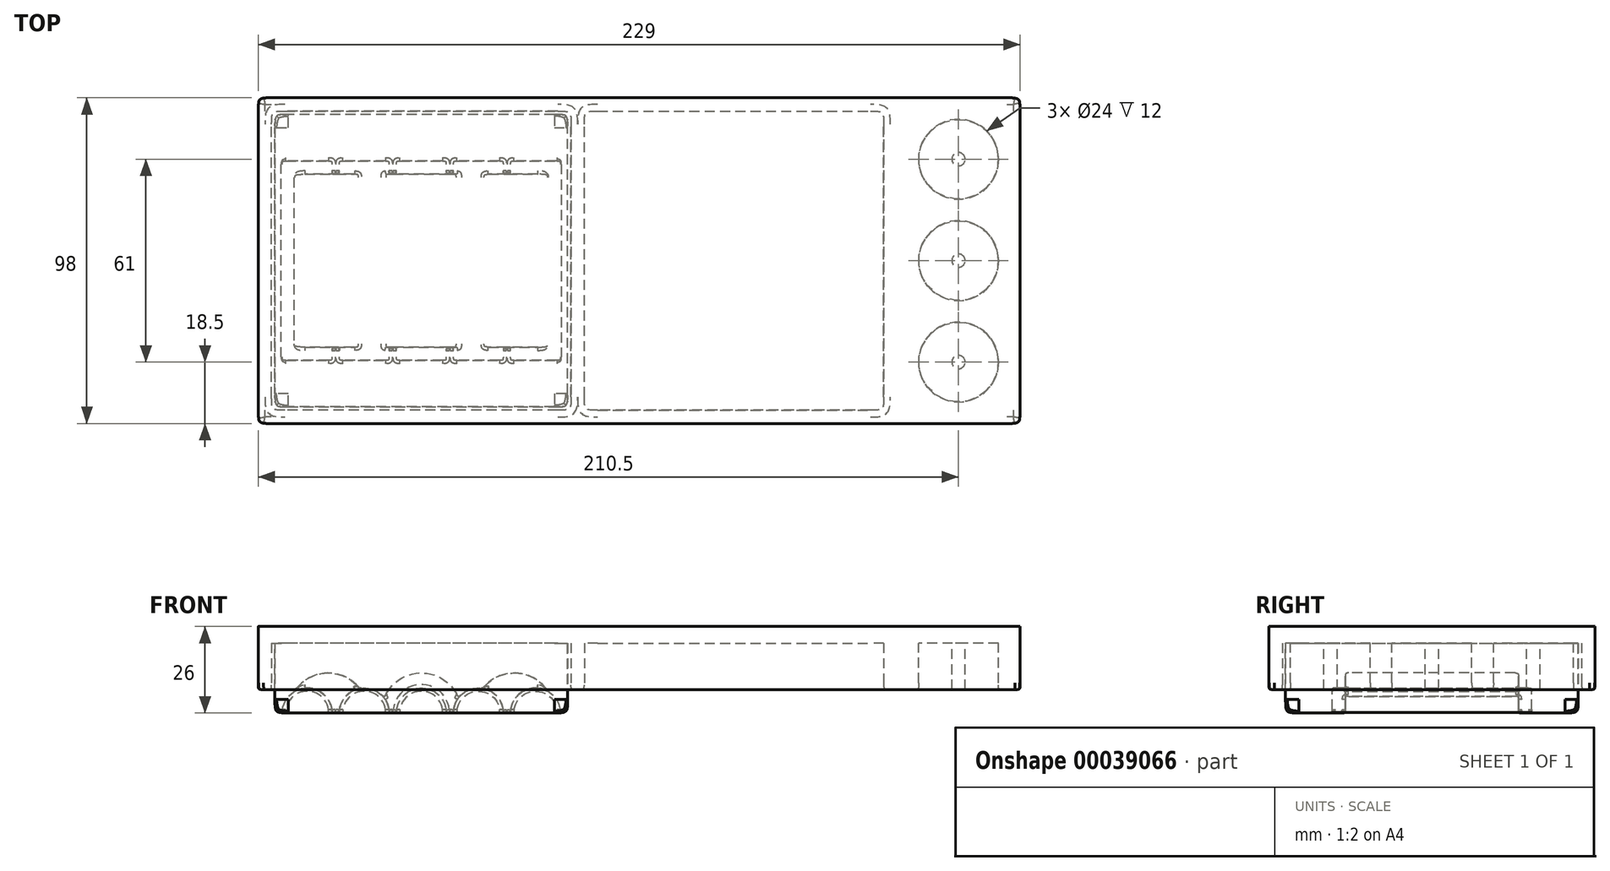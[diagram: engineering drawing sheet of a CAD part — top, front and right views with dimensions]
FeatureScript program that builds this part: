
annotation { "Feature Type Name" : "Feature", "Feature Type Description" : "" }
export const myFeature = defineFeature(function(context is Context, id is Id, definition is map)
    precondition{}
    {
        {
            var Q0;
            Q0=qCreatedBy(makeId("Top.planeOp"),FACE);
            var sketch = newSketch(context, id + "F0", { "sketchPlane" : qUnion([Q0])});
            skLineSegment(sketch, "E0.rect.bottom", {"start": v(44, -44) * mm, "end": v(-44, -44) * mm});
            skLineSegment(sketch, "E0.rect.top", {"start": v(44, 44) * mm, "end": v(-44, 44) * mm});
            skLineSegment(sketch, "E0.rect.left", {"start": v(44, -44) * mm, "end": v(44, 44) * mm});
            skLineSegment(sketch, "E0.rect.right", {"start": v(-44, -44) * mm, "end": v(-44, 44) * mm});
            skPoint(sketch, "E0.rect.middle", {"position": v(0, 0) * mm});
            skLineSegment(sketch, "E1.rect.bottom", {"start": v(12, -26) * mm, "end": v(-12, -26) * mm});
            skLineSegment(sketch, "E1.rect.top", {"start": v(12, 26) * mm, "end": v(-12, 26) * mm});
            skLineSegment(sketch, "E1.rect.left", {"start": v(12, -26) * mm, "end": v(12, 26) * mm});
            skLineSegment(sketch, "E1.rect.right", {"start": v(-12, -26) * mm, "end": v(-12, 26) * mm});
            skLineSegment(sketch, "E2.rect.bottom", {"start": v(40, -26) * mm, "end": v(16, -26) * mm});
            skLineSegment(sketch, "E2.rect.top", {"start": v(40, 26) * mm, "end": v(16, 26) * mm});
            skLineSegment(sketch, "E2.rect.left", {"start": v(40, -26) * mm, "end": v(40, 26) * mm});
            skLineSegment(sketch, "E2.rect.right", {"start": v(16, -26) * mm, "end": v(16, 26) * mm});
            skPoint(sketch, "E2.rect.middle", {"position": v(28, 0) * mm});
            skLineSegment(sketch, "E3.rect.bottom", {"start": v(-16, -26) * mm, "end": v(-40, -26) * mm});
            skLineSegment(sketch, "E3.rect.top", {"start": v(-16, 26) * mm, "end": v(-40, 26) * mm});
            skLineSegment(sketch, "E3.rect.left", {"start": v(-16, -26) * mm, "end": v(-16, 26) * mm});
            skLineSegment(sketch, "E3.rect.right", {"start": v(-40, -26) * mm, "end": v(-40, 26) * mm});
            skPoint(sketch, "E3.rect.middle", {"position": v(-28, 0) * mm});
            skLineSegment(sketch, "E4.rect.bottom", {"start": v(-7.5, -30) * mm, "end": v(7.5, -30) * mm});
            skLineSegment(sketch, "E4.rect.top", {"start": v(-7.5, 30) * mm, "end": v(7.5, 30) * mm});
            skLineSegment(sketch, "E4.rect.left", {"start": v(-7.5, -30) * mm, "end": v(-7.5, 30) * mm});
            skLineSegment(sketch, "E4.rect.right", {"start": v(7.5, -30) * mm, "end": v(7.5, 30) * mm});
            skLineSegment(sketch, "E5.rect.bottom", {"start": v(24.66, -30) * mm, "end": v(9.66, -30) * mm});
            skLineSegment(sketch, "E5.rect.top", {"start": v(24.66, 30) * mm, "end": v(9.66, 30) * mm});
            skLineSegment(sketch, "E5.rect.left", {"start": v(24.66, -30) * mm, "end": v(24.66, 30) * mm});
            skLineSegment(sketch, "E5.rect.right", {"start": v(9.66, -30) * mm, "end": v(9.66, 30) * mm});
            skPoint(sketch, "E5.rect.middle", {"position": v(17.16, 0) * mm});
            skLineSegment(sketch, "E6.rect.bottom", {"start": v(26.82, -30) * mm, "end": v(41.82, -30) * mm});
            skLineSegment(sketch, "E6.rect.top", {"start": v(26.82, 30) * mm, "end": v(41.82, 30) * mm});
            skLineSegment(sketch, "E6.rect.left", {"start": v(26.82, -30) * mm, "end": v(26.82, 30) * mm});
            skLineSegment(sketch, "E6.rect.right", {"start": v(41.82, -30) * mm, "end": v(41.82, 30) * mm});
            skPoint(sketch, "E6.rect.middle", {"position": v(34.32, 0) * mm});
            skLineSegment(sketch, "E7.rect.bottom", {"start": v(-9.66, -30) * mm, "end": v(-24.66, -30) * mm});
            skLineSegment(sketch, "E7.rect.top", {"start": v(-9.66, 30) * mm, "end": v(-24.66, 30) * mm});
            skLineSegment(sketch, "E7.rect.left", {"start": v(-9.66, -30) * mm, "end": v(-9.66, 30) * mm});
            skLineSegment(sketch, "E7.rect.right", {"start": v(-24.66, -30) * mm, "end": v(-24.66, 30) * mm});
            skPoint(sketch, "E7.rect.middle", {"position": v(-17.16, 0) * mm});
            skLineSegment(sketch, "E8.rect.bottom", {"start": v(-26.82, -30) * mm, "end": v(-41.82, -30) * mm});
            skLineSegment(sketch, "E8.rect.top", {"start": v(-26.82, 30) * mm, "end": v(-41.82, 30) * mm});
            skLineSegment(sketch, "E8.rect.left", {"start": v(-26.82, -30) * mm, "end": v(-26.82, 30) * mm});
            skLineSegment(sketch, "E8.rect.right", {"start": v(-41.82, -30) * mm, "end": v(-41.82, 30) * mm});
            skPoint(sketch, "E8.rect.middle", {"position": v(-34.32, 0) * mm});
            skLineSegment(sketch, "E9", {"start": v(44, 0) * mm, "end": v(41.82, 0) * mm, "construction": true});
            skLineSegment(sketch, "E10", {"start": v(26.82, 0) * mm, "end": v(24.66, 0) * mm, "construction": true});
            skLineSegment(sketch, "E11", {"start": v(9.66, 0) * mm, "end": v(7.5, 0) * mm, "construction": true});
            skLineSegment(sketch, "E12", {"start": v(-7.5, 0) * mm, "end": v(-9.66, 0) * mm, "construction": true});
            skLineSegment(sketch, "E13", {"start": v(-24.66, 0) * mm, "end": v(-26.82, 0) * mm, "construction": true});
            skLineSegment(sketch, "E14", {"start": v(-41.82, 0) * mm, "end": v(-44, 0) * mm, "construction": true});
            skSolve(sketch);
        }
        {
            var Q0;
            Q0=makeQuery(id+"F0.imprint","IMPRINT",FACE,{"disambiguationData":[TD([[makeQuery(id+"F0.imprint","IMPRINT",EDGE,{"derivedFrom":sQuery(id+"F0.wireOp",EDGE,"E0.rect.bottom")}),-1.0]])]});
            var Q1;
            {var subQ6=sQuery(id+"F0.wireOp",EDGE,"E2.rect.left");Q1=makeQuery(id+"F0.imprint","IMPRINT",FACE,{"disambiguationData":[TD([[makeQuery(id+"F0.imprint","IMPRINT",EDGE,{"derivedFrom":subQ6}),-1.0]])]});}
            var Q2;
            {var subQ5=sQuery(id+"F0.wireOp",EDGE,"E2.rect.left");Q2=makeQuery(id+"F0.imprint","IMPRINT",FACE,{"disambiguationData":[TD([[makeQuery(id+"F0.imprint","IMPRINT",EDGE,{"derivedFrom":subQ5}),1.0]])]});}
            var Q3;
            {var subQ3=sQuery(id+"F0.wireOp",EDGE,"E2.rect.bottom");var subQ5=sQuery(id+"F0.wireOp",EDGE,"E6.rect.left");var subQ7=makeQuery(id+"F0.imprint","INTERSECT",VERTEX,{"derivedFrom":[subQ3,subQ5]});Q3=makeQuery(id+"F0.imprint","IMPRINT",FACE,{"disambiguationData":[TD([[makeQuery(id+"F0.imprint","IMPRINT",EDGE,{"disambiguationData":[TD([[subQ7,-1.0]])],"derivedFrom":subQ3}),-1.0]])]});}
            var Q4;
            {var subQ11=sQuery(id+"F0.wireOp",EDGE,"E1.rect.left");Q4=makeQuery(id+"F0.imprint","IMPRINT",FACE,{"disambiguationData":[TD([[makeQuery(id+"F0.imprint","IMPRINT",EDGE,{"derivedFrom":subQ11}),-1.0]])]});}
            var Q5;
            {var subQ5=sQuery(id+"F0.wireOp",EDGE,"E2.rect.right");Q5=makeQuery(id+"F0.imprint","IMPRINT",FACE,{"disambiguationData":[TD([[makeQuery(id+"F0.imprint","IMPRINT",EDGE,{"derivedFrom":subQ5}),-1.0]])]});}
            var Q6;
            {var subQ5=sQuery(id+"F0.wireOp",EDGE,"E1.rect.left");Q6=makeQuery(id+"F0.imprint","IMPRINT",FACE,{"disambiguationData":[TD([[makeQuery(id+"F0.imprint","IMPRINT",EDGE,{"derivedFrom":subQ5}),1.0]])]});}
            var Q7;
            {var subQ0=sQuery(id+"F0.wireOp",EDGE,"E5.rect.right");var subQ3=sQuery(id+"F0.wireOp",EDGE,"E1.rect.bottom");var subQ4=makeQuery(id+"F0.imprint","INTERSECT",VERTEX,{"derivedFrom":[subQ3,subQ0]});Q7=makeQuery(id+"F0.imprint","IMPRINT",FACE,{"disambiguationData":[TD([[makeQuery(id+"F0.imprint","IMPRINT",EDGE,{"disambiguationData":[TD([[subQ4,-1.0]])],"derivedFrom":subQ3}),-1.0]])]});}
            var Q8;
            {var subQ0=sQuery(id+"F0.wireOp",EDGE,"E4.rect.right");var subQ3=sQuery(id+"F0.wireOp",EDGE,"E1.rect.bottom");var subQ4=makeQuery(id+"F0.imprint","INTERSECT",VERTEX,{"derivedFrom":[subQ3,subQ0]});Q8=makeQuery(id+"F0.imprint","IMPRINT",FACE,{"disambiguationData":[TD([[makeQuery(id+"F0.imprint","IMPRINT",EDGE,{"disambiguationData":[TD([[subQ4,-1.0]])],"derivedFrom":subQ3}),-1.0]])]});}
            var Q9;
            {var subQ0=sQuery(id+"F0.wireOp",EDGE,"E4.rect.bottom");Q9=makeQuery(id+"F0.imprint","IMPRINT",FACE,{"disambiguationData":[TD([[makeQuery(id+"F0.imprint","IMPRINT",EDGE,{"derivedFrom":subQ0}),1.0]])]});}
            var Q10;
            {var subQ3=sQuery(id+"F0.wireOp",EDGE,"E4.rect.top");Q10=makeQuery(id+"F0.imprint","IMPRINT",FACE,{"disambiguationData":[TD([[makeQuery(id+"F0.imprint","IMPRINT",EDGE,{"derivedFrom":subQ3}),-1.0]])]});}
            var Q11;
            {var subQ3=sQuery(id+"F0.wireOp",EDGE,"E1.rect.bottom");var subQ5=sQuery(id+"F0.wireOp",EDGE,"E4.rect.left");var subQ7=makeQuery(id+"F0.imprint","INTERSECT",VERTEX,{"derivedFrom":[subQ3,subQ5]});Q11=makeQuery(id+"F0.imprint","IMPRINT",FACE,{"disambiguationData":[TD([[makeQuery(id+"F0.imprint","IMPRINT",EDGE,{"disambiguationData":[TD([[subQ7,-1.0]])],"derivedFrom":subQ3}),-1.0]])]});}
            var Q12;
            {var subQ5=sQuery(id+"F0.wireOp",EDGE,"E1.rect.right");Q12=makeQuery(id+"F0.imprint","IMPRINT",FACE,{"disambiguationData":[TD([[makeQuery(id+"F0.imprint","IMPRINT",EDGE,{"derivedFrom":subQ5}),-1.0]])]});}
            var Q13;
            {var subQ5=sQuery(id+"F0.wireOp",EDGE,"E1.rect.right");Q13=makeQuery(id+"F0.imprint","IMPRINT",FACE,{"disambiguationData":[TD([[makeQuery(id+"F0.imprint","IMPRINT",EDGE,{"derivedFrom":subQ5}),1.0]])]});}
            var Q14;
            {var subQ5=sQuery(id+"F0.wireOp",EDGE,"E3.rect.left");Q14=makeQuery(id+"F0.imprint","IMPRINT",FACE,{"disambiguationData":[TD([[makeQuery(id+"F0.imprint","IMPRINT",EDGE,{"derivedFrom":subQ5}),1.0]])]});}
            var Q15;
            {var subQ3=sQuery(id+"F0.wireOp",EDGE,"E3.rect.bottom");var subQ5=sQuery(id+"F0.wireOp",EDGE,"E7.rect.right");var subQ7=makeQuery(id+"F0.imprint","INTERSECT",VERTEX,{"derivedFrom":[subQ3,subQ5]});Q15=makeQuery(id+"F0.imprint","IMPRINT",FACE,{"disambiguationData":[TD([[makeQuery(id+"F0.imprint","IMPRINT",EDGE,{"disambiguationData":[TD([[subQ7,-1.0]])],"derivedFrom":subQ3}),-1.0]])]});}
            var Q16;
            {var subQ5=sQuery(id+"F0.wireOp",EDGE,"E3.rect.right");Q16=makeQuery(id+"F0.imprint","IMPRINT",FACE,{"disambiguationData":[TD([[makeQuery(id+"F0.imprint","IMPRINT",EDGE,{"derivedFrom":subQ5}),-1.0]])]});}
            var Q17;
            {var subQ7=sQuery(id+"F0.wireOp",EDGE,"E3.rect.right");Q17=makeQuery(id+"F0.imprint","IMPRINT",FACE,{"disambiguationData":[TD([[makeQuery(id+"F0.imprint","IMPRINT",EDGE,{"derivedFrom":subQ7}),1.0]])]});}
            extrude(context, id + "F1", {"entities" : qUnion([Q0, Q1, Q2, Q3, Q4, Q5, Q6, Q7, Q8, Q9, Q10, Q11, Q12, Q13, Q14, Q15, Q16, Q17]), "depth" : 21 * mm});
        }
        {
            var Q0;
            Q0=makeQuery(id+"F0.imprint","IMPRINT",FACE,{"disambiguationData":[TD([[makeQuery(id+"F0.imprint","IMPRINT",EDGE,{"derivedFrom":sQuery(id+"F0.wireOp",EDGE,"E0.rect.bottom")}),-1.0]])]});
            var sketch = newSketch(context, id + "F2", { "sketchPlane" : qUnion([Q0])});
            skLineSegment(sketch, "E15.rect.bottom", {"start": v(16, -26) * mm, "end": v(40, -26) * mm});
            skLineSegment(sketch, "E15.rect.top", {"start": v(16, 26) * mm, "end": v(40, 26) * mm});
            skLineSegment(sketch, "E15.rect.left", {"start": v(16, -26) * mm, "end": v(16, 26) * mm});
            skLineSegment(sketch, "E15.rect.right", {"start": v(40, -26) * mm, "end": v(40, 26) * mm});
            skPoint(sketch, "E15.rect.middle", {"position": v(28, 0) * mm});
            skLineSegment(sketch, "E16.rect.bottom", {"start": v(12, -26) * mm, "end": v(-12, -26) * mm});
            skLineSegment(sketch, "E16.rect.top", {"start": v(12, 26) * mm, "end": v(-12, 26) * mm});
            skLineSegment(sketch, "E16.rect.left", {"start": v(12, -26) * mm, "end": v(12, 26) * mm});
            skLineSegment(sketch, "E16.rect.right", {"start": v(-12, -26) * mm, "end": v(-12, 26) * mm});
            skPoint(sketch, "E16.rect.middle", {"position": v(0, 0) * mm});
            skLineSegment(sketch, "E17.rect.bottom", {"start": v(-40, 26) * mm, "end": v(-16, 26) * mm});
            skLineSegment(sketch, "E17.rect.top", {"start": v(-40, -26) * mm, "end": v(-16, -26) * mm});
            skLineSegment(sketch, "E17.rect.left", {"start": v(-40, 26) * mm, "end": v(-40, -26) * mm});
            skLineSegment(sketch, "E17.rect.right", {"start": v(-16, 26) * mm, "end": v(-16, -26) * mm});
            skPoint(sketch, "E17.rect.middle", {"position": v(-28, 0) * mm});
            skLineSegment(sketch, "E18", {"start": v(28, 26) * mm, "end": v(28, -26) * mm});
            skLineSegment(sketch, "E19", {"start": v(0, 26) * mm, "end": v(0, -26) * mm});
            skLineSegment(sketch, "E20", {"start": v(-28, 26) * mm, "end": v(-28, -26) * mm});
            skSolve(sketch);
        }
        {
            var Q0;
            {var subQ2=sQuery(id+"F2.wireOp",EDGE,"E15.rect.right");Q0=makeQuery(id+"F2.imprint","IMPRINT",FACE,{"disambiguationData":[TD([[makeQuery(id+"F2.imprint","IMPRINT",EDGE,{"derivedFrom":subQ2}),1.0]])]});}
            var Q1;
            Q1=sQuery(id+"F2.wireOp",EDGE,"E18");
            revolve(context, id + "F3", {"operationType" : NewBodyOperationType.REMOVE, "entities" : qUnion([Q0]), "axis" : qUnion([Q1]), "revolveType" : RevolveType.FULL, "oppositeDirection" : true});
        }
        {
            var Q0;
            {var subQ1=sQuery(id+"F2.wireOp",EDGE,"E16.rect.left");Q0=makeQuery(id+"F2.imprint","IMPRINT",FACE,{"disambiguationData":[TD([[makeQuery(id+"F2.imprint","IMPRINT",EDGE,{"derivedFrom":subQ1}),1.0]])]});}
            var Q1;
            Q1=sQuery(id+"F2.wireOp",EDGE,"E19");
            revolve(context, id + "F4", {"operationType" : NewBodyOperationType.REMOVE, "entities" : qUnion([Q0]), "axis" : qUnion([Q1]), "revolveType" : RevolveType.FULL, "oppositeDirection" : true});
        }
        {
            var Q0;
            {var subQ0=sQuery(id+"F2.wireOp",EDGE,"E17.rect.right");Q0=makeQuery(id+"F2.imprint","IMPRINT",FACE,{"disambiguationData":[TD([[makeQuery(id+"F2.imprint","IMPRINT",EDGE,{"derivedFrom":subQ0}),-1.0]])]});}
            var Q1;
            Q1=sQuery(id+"F2.wireOp",EDGE,"E20");
            revolve(context, id + "F5", {"operationType" : NewBodyOperationType.REMOVE, "entities" : qUnion([Q0]), "axis" : qUnion([Q1]), "revolveType" : RevolveType.FULL, "oppositeDirection" : true});
        }
        {
            var Q0;
            Q0=makeQuery(id+"F0.imprint","IMPRINT",FACE,{"disambiguationData":[TD([[makeQuery(id+"F0.imprint","IMPRINT",EDGE,{"derivedFrom":sQuery(id+"F0.wireOp",EDGE,"E0.rect.bottom")}),-1.0]])]});
            var sketch = newSketch(context, id + "F6", { "sketchPlane" : qUnion([Q0])});
            skLineSegment(sketch, "E21.rect.bottom", {"start": v(41.82, 30) * mm, "end": v(26.82, 30) * mm});
            skLineSegment(sketch, "E21.rect.top", {"start": v(41.82, -30) * mm, "end": v(26.82, -30) * mm});
            skLineSegment(sketch, "E21.rect.left", {"start": v(41.82, 30) * mm, "end": v(41.82, -30) * mm});
            skLineSegment(sketch, "E21.rect.right", {"start": v(26.82, 30) * mm, "end": v(26.82, -30) * mm});
            skPoint(sketch, "E21.rect.middle", {"position": v(34.32, 0) * mm});
            skLineSegment(sketch, "E22.rect.bottom", {"start": v(24.66, 30) * mm, "end": v(9.66, 30) * mm});
            skLineSegment(sketch, "E22.rect.top", {"start": v(24.66, -30) * mm, "end": v(9.66, -30) * mm});
            skLineSegment(sketch, "E22.rect.left", {"start": v(24.66, 30) * mm, "end": v(24.66, -30) * mm});
            skLineSegment(sketch, "E22.rect.right", {"start": v(9.66, 30) * mm, "end": v(9.66, -30) * mm});
            skPoint(sketch, "E22.rect.middle", {"position": v(17.16, 0) * mm});
            skLineSegment(sketch, "E23.rect.bottom", {"start": v(-7.5, 30) * mm, "end": v(7.5, 30) * mm});
            skLineSegment(sketch, "E23.rect.top", {"start": v(-7.5, -30) * mm, "end": v(7.5, -30) * mm});
            skLineSegment(sketch, "E23.rect.left", {"start": v(-7.5, 30) * mm, "end": v(-7.5, -30) * mm});
            skLineSegment(sketch, "E23.rect.right", {"start": v(7.5, 30) * mm, "end": v(7.5, -30) * mm});
            skPoint(sketch, "E23.rect.middle", {"position": v(0, 0) * mm});
            skLineSegment(sketch, "E24.rect.bottom", {"start": v(-24.66, 30) * mm, "end": v(-9.66, 30) * mm});
            skLineSegment(sketch, "E24.rect.top", {"start": v(-24.66, -30) * mm, "end": v(-9.66, -30) * mm});
            skLineSegment(sketch, "E24.rect.left", {"start": v(-24.66, 30) * mm, "end": v(-24.66, -30) * mm});
            skLineSegment(sketch, "E24.rect.right", {"start": v(-9.66, 30) * mm, "end": v(-9.66, -30) * mm});
            skPoint(sketch, "E24.rect.middle", {"position": v(-17.16, 0) * mm});
            skLineSegment(sketch, "E25.rect.bottom", {"start": v(-41.82, 30) * mm, "end": v(-26.82, 30) * mm});
            skLineSegment(sketch, "E25.rect.top", {"start": v(-41.82, -30) * mm, "end": v(-26.82, -30) * mm});
            skLineSegment(sketch, "E25.rect.left", {"start": v(-41.82, 30) * mm, "end": v(-41.82, -30) * mm});
            skLineSegment(sketch, "E25.rect.right", {"start": v(-26.82, 30) * mm, "end": v(-26.82, -30) * mm});
            skPoint(sketch, "E25.rect.middle", {"position": v(-34.32, 0) * mm});
            skLineSegment(sketch, "E26", {"start": v(34.32, 30) * mm, "end": v(34.32, -30) * mm});
            skLineSegment(sketch, "E27", {"start": v(17.16, -30) * mm, "end": v(17.16, 30) * mm});
            skLineSegment(sketch, "E28", {"start": v(0, -30) * mm, "end": v(0, 30) * mm});
            skLineSegment(sketch, "E29", {"start": v(-17.16, -30) * mm, "end": v(-17.16, 30) * mm});
            skLineSegment(sketch, "E30", {"start": v(-34.32, -30) * mm, "end": v(-34.32, 30) * mm});
            skSolve(sketch);
        }
        {
            var Q0;
            {var subQ8=sQuery(id+"F6.wireOp",EDGE,"E26");Q0=makeQuery(id+"F6.imprint","IMPRINT",FACE,{"disambiguationData":[TD([[makeQuery(id+"F6.imprint","IMPRINT",EDGE,{"derivedFrom":subQ8}),-1.0]])]});}
            var Q1;
            Q1=sQuery(id+"F6.wireOp",EDGE,"E26");
            revolve(context, id + "F7", {"operationType" : NewBodyOperationType.REMOVE, "entities" : qUnion([Q0]), "axis" : qUnion([Q1]), "revolveType" : RevolveType.FULL, "oppositeDirection" : true});
        }
        {
            var Q0;
            {var subQ8=sQuery(id+"F6.wireOp",EDGE,"E27");Q0=makeQuery(id+"F6.imprint","IMPRINT",FACE,{"disambiguationData":[TD([[makeQuery(id+"F6.imprint","IMPRINT",EDGE,{"derivedFrom":subQ8}),1.0]])]});}
            var Q1;
            Q1=sQuery(id+"F6.wireOp",EDGE,"E27");
            revolve(context, id + "F8", {"operationType" : NewBodyOperationType.REMOVE, "entities" : qUnion([Q0]), "axis" : qUnion([Q1]), "revolveType" : RevolveType.FULL, "oppositeDirection" : true});
        }
        {
            var Q0;
            {var subQ0=sQuery(id+"F6.wireOp",EDGE,"E28");Q0=makeQuery(id+"F6.imprint","IMPRINT",FACE,{"disambiguationData":[TD([[makeQuery(id+"F6.imprint","IMPRINT",EDGE,{"derivedFrom":subQ0}),1.0]])]});}
            var Q1;
            Q1=sQuery(id+"F6.wireOp",EDGE,"E28");
            revolve(context, id + "F9", {"operationType" : NewBodyOperationType.REMOVE, "entities" : qUnion([Q0]), "axis" : qUnion([Q1]), "revolveType" : RevolveType.FULL, "oppositeDirection" : true});
        }
        {
            var Q0;
            {var subQ7=sQuery(id+"F6.wireOp",EDGE,"E29");Q0=makeQuery(id+"F6.imprint","IMPRINT",FACE,{"disambiguationData":[TD([[makeQuery(id+"F6.imprint","IMPRINT",EDGE,{"derivedFrom":subQ7}),-1.0]])]});}
            var Q1;
            Q1=sQuery(id+"F6.wireOp",EDGE,"E29");
            revolve(context, id + "F10", {"operationType" : NewBodyOperationType.REMOVE, "entities" : qUnion([Q0]), "axis" : qUnion([Q1]), "revolveType" : RevolveType.FULL, "oppositeDirection" : true});
        }
        {
            var Q0;
            {var subQ8=sQuery(id+"F6.wireOp",EDGE,"E30");Q0=makeQuery(id+"F6.imprint","IMPRINT",FACE,{"disambiguationData":[TD([[makeQuery(id+"F6.imprint","IMPRINT",EDGE,{"derivedFrom":subQ8}),-1.0]])]});}
            var Q1;
            Q1=sQuery(id+"F6.wireOp",EDGE,"E30");
            revolve(context, id + "F11", {"operationType" : NewBodyOperationType.REMOVE, "entities" : qUnion([Q0]), "axis" : qUnion([Q1]), "revolveType" : RevolveType.FULL, "oppositeDirection" : true});
        }
        {
            var Q0;
            Q0=makeQuery(id+"F10.boolean.opBoolean","INTERSECT",EDGE,{"derivedFrom":[makeQuery(id+"F5.boolean.opBoolean","COPY",FACE,{"derivedFrom":makeQuery(id+"F5.opRevolve","SWEPT_FACE",FACE,{"disambiguationData":[OSD([sQuery(id+"F2.wireOp",EDGE,"E17.rect.right")])]})}),makeQuery(id+"F10.opRevolve","SWEPT_FACE",FACE,{"disambiguationData":[OSD([sQuery(id+"F6.wireOp",EDGE,"E24.rect.right")])]})]});
            var Q1;
            Q1=makeQuery(id+"F10.boolean.opBoolean","INTERSECT",EDGE,{"derivedFrom":[makeQuery(id+"F4.boolean.opBoolean","COPY",FACE,{"derivedFrom":makeQuery(id+"F4.opRevolve","SWEPT_FACE",FACE,{"disambiguationData":[OSD([sQuery(id+"F2.wireOp",EDGE,"E16.rect.left")])]})}),makeQuery(id+"F10.opRevolve","SWEPT_FACE",FACE,{"disambiguationData":[OSD([sQuery(id+"F6.wireOp",EDGE,"E24.rect.right")])]})]});
            var Q2;
            Q2=makeQuery(id+"F11.boolean.opBoolean","INTERSECT",EDGE,{"derivedFrom":[makeQuery(id+"F5.boolean.opBoolean","COPY",FACE,{"derivedFrom":makeQuery(id+"F5.opRevolve","SWEPT_FACE",FACE,{"disambiguationData":[OSD([sQuery(id+"F2.wireOp",EDGE,"E17.rect.right")])]})}),makeQuery(id+"F11.opRevolve","SWEPT_FACE",FACE,{"disambiguationData":[OSD([sQuery(id+"F6.wireOp",EDGE,"E25.rect.right")])]})]});
            var Q3;
            Q3=makeQuery(id+"F11.boolean.opBoolean","INTERSECT",EDGE,{"disambiguationData":[OD(2.0)],"derivedFrom":[makeQuery(id+"F1.opExtrude","CAP_FACE",FACE,{"disambiguationData":[OSD([sQuery(id+"F0.wireOp",EDGE,"E0.rect.bottom"),sQuery(id+"F0.wireOp",EDGE,"E0.rect.top"),sQuery(id+"F0.wireOp",EDGE,"E0.rect.left"),sQuery(id+"F0.wireOp",EDGE,"E0.rect.right")])],"isStart":true}),makeQuery(id+"F11.opRevolve","SWEPT_FACE",FACE,{"disambiguationData":[OSD([sQuery(id+"F6.wireOp",EDGE,"E25.rect.right")])]})]});
            var Q4;
            Q4=makeQuery(id+"F5.boolean.opBoolean","COPY",EDGE,{"derivedFrom":makeQuery(id+"F5.opRevolve","SWEPT_EDGE",EDGE,{"disambiguationData":[OSD([sQuery(id+"F2.wireOp",EDGE,"E17.rect.top"),sQuery(id+"F2.wireOp",EDGE,"E17.rect.right")])]})});
            var Q5;
            Q5=makeQuery(id+"F11.boolean.opBoolean","INTERSECT",EDGE,{"derivedFrom":[makeQuery(id+"F5.boolean.opBoolean","COPY",FACE,{"derivedFrom":makeQuery(id+"F5.opRevolve","SWEPT_FACE",FACE,{"disambiguationData":[OSD([sQuery(id+"F2.wireOp",EDGE,"E17.rect.top")])]})}),makeQuery(id+"F11.opRevolve","SWEPT_FACE",FACE,{"disambiguationData":[OSD([sQuery(id+"F6.wireOp",EDGE,"E25.rect.right")])]})]});
            var Q6;
            Q6=makeQuery(id+"F5.boolean.opBoolean","INTERSECT",EDGE,{"derivedFrom":[makeQuery(id+"F1.opExtrude","CAP_FACE",FACE,{"disambiguationData":[OSD([sQuery(id+"F0.wireOp",EDGE,"E0.rect.bottom"),sQuery(id+"F0.wireOp",EDGE,"E0.rect.top"),sQuery(id+"F0.wireOp",EDGE,"E0.rect.left"),sQuery(id+"F0.wireOp",EDGE,"E0.rect.right")])],"isStart":true}),makeQuery(id+"F5.opRevolve","SWEPT_FACE",FACE,{"disambiguationData":[OSD([sQuery(id+"F2.wireOp",EDGE,"E17.rect.top")])]})]});
            var Q7;
            Q7=makeQuery(id+"F10.boolean.opBoolean","INTERSECT",EDGE,{"derivedFrom":[makeQuery(id+"F5.boolean.opBoolean","COPY",FACE,{"derivedFrom":makeQuery(id+"F5.opRevolve","SWEPT_FACE",FACE,{"disambiguationData":[OSD([sQuery(id+"F2.wireOp",EDGE,"E17.rect.top")])]})}),makeQuery(id+"F10.opRevolve","SWEPT_FACE",FACE,{"disambiguationData":[OSD([sQuery(id+"F6.wireOp",EDGE,"E24.rect.right")])]})]});
            var Q8;
            Q8=makeQuery(id+"F11.boolean.opBoolean","INTERSECT",EDGE,{"disambiguationData":[OD(1.0)],"derivedFrom":[makeQuery(id+"F1.opExtrude","CAP_FACE",FACE,{"disambiguationData":[OSD([sQuery(id+"F0.wireOp",EDGE,"E0.rect.bottom"),sQuery(id+"F0.wireOp",EDGE,"E0.rect.top"),sQuery(id+"F0.wireOp",EDGE,"E0.rect.left"),sQuery(id+"F0.wireOp",EDGE,"E0.rect.right")])],"isStart":true}),makeQuery(id+"F11.opRevolve","SWEPT_FACE",FACE,{"disambiguationData":[OSD([sQuery(id+"F6.wireOp",EDGE,"E25.rect.right")])]})]});
            var Q9;
            Q9=makeQuery(id+"F11.boolean.opBoolean","COPY",EDGE,{"derivedFrom":makeQuery(id+"F11.opRevolve","SWEPT_EDGE",EDGE,{"disambiguationData":[OSD([sQuery(id+"F6.wireOp",EDGE,"E25.rect.top"),sQuery(id+"F6.wireOp",EDGE,"E25.rect.right")])]})});
            var Q10;
            Q10=makeQuery(id+"F11.boolean.opBoolean","INTERSECT",EDGE,{"derivedFrom":[makeQuery(id+"F1.opExtrude","CAP_FACE",FACE,{"disambiguationData":[OSD([sQuery(id+"F0.wireOp",EDGE,"E0.rect.bottom"),sQuery(id+"F0.wireOp",EDGE,"E0.rect.top"),sQuery(id+"F0.wireOp",EDGE,"E0.rect.left"),sQuery(id+"F0.wireOp",EDGE,"E0.rect.right")])],"isStart":true}),makeQuery(id+"F11.opRevolve","SWEPT_FACE",FACE,{"disambiguationData":[OSD([sQuery(id+"F6.wireOp",EDGE,"E25.rect.top")])]})]});
            var Q11;
            Q11=makeQuery(id+"F10.boolean.opBoolean","COPY",EDGE,{"derivedFrom":makeQuery(id+"F10.opRevolve","SWEPT_EDGE",EDGE,{"disambiguationData":[OSD([sQuery(id+"F6.wireOp",EDGE,"E24.rect.top"),sQuery(id+"F6.wireOp",EDGE,"E24.rect.right")])]})});
            var Q12;
            Q12=makeQuery(id+"F10.boolean.opBoolean","INTERSECT",EDGE,{"derivedFrom":[makeQuery(id+"F1.opExtrude","CAP_FACE",FACE,{"disambiguationData":[OSD([sQuery(id+"F0.wireOp",EDGE,"E0.rect.bottom"),sQuery(id+"F0.wireOp",EDGE,"E0.rect.top"),sQuery(id+"F0.wireOp",EDGE,"E0.rect.left"),sQuery(id+"F0.wireOp",EDGE,"E0.rect.right")])],"isStart":true}),makeQuery(id+"F10.opRevolve","SWEPT_FACE",FACE,{"disambiguationData":[OSD([sQuery(id+"F6.wireOp",EDGE,"E24.rect.top")])]})]});
            var Q13;
            Q13=makeQuery(id+"F10.boolean.opBoolean","INTERSECT",EDGE,{"disambiguationData":[OD(2.0)],"derivedFrom":[makeQuery(id+"F1.opExtrude","CAP_FACE",FACE,{"disambiguationData":[OSD([sQuery(id+"F0.wireOp",EDGE,"E0.rect.bottom"),sQuery(id+"F0.wireOp",EDGE,"E0.rect.top"),sQuery(id+"F0.wireOp",EDGE,"E0.rect.left"),sQuery(id+"F0.wireOp",EDGE,"E0.rect.right")])],"isStart":true}),makeQuery(id+"F10.opRevolve","SWEPT_FACE",FACE,{"disambiguationData":[OSD([sQuery(id+"F6.wireOp",EDGE,"E24.rect.right")])]})]});
            var Q14;
            Q14=makeQuery(id+"F10.boolean.opBoolean","INTERSECT",EDGE,{"derivedFrom":[makeQuery(id+"F4.boolean.opBoolean","COPY",FACE,{"derivedFrom":makeQuery(id+"F4.opRevolve","SWEPT_FACE",FACE,{"disambiguationData":[OSD([sQuery(id+"F2.wireOp",EDGE,"E16.rect.bottom")])]})}),makeQuery(id+"F10.opRevolve","SWEPT_FACE",FACE,{"disambiguationData":[OSD([sQuery(id+"F6.wireOp",EDGE,"E24.rect.right")])]})]});
            var Q15;
            {var subQ0=makeQuery(id+"F1.opExtrude","CAP_FACE",FACE,{"disambiguationData":[OSD([sQuery(id+"F0.wireOp",EDGE,"E0.rect.bottom"),sQuery(id+"F0.wireOp",EDGE,"E0.rect.top"),sQuery(id+"F0.wireOp",EDGE,"E0.rect.left"),sQuery(id+"F0.wireOp",EDGE,"E0.rect.right")])],"isStart":true});var subQ1=makeQuery(id+"F4.opRevolve","SWEPT_FACE",FACE,{"disambiguationData":[OSD([sQuery(id+"F2.wireOp",EDGE,"E16.rect.bottom")])]});Q15=makeQuery(id+"F9.boolean.opBoolean","SPLIT",EDGE,{"disambiguationData":[TD([makeQuery(id+"F4.boolean.opBoolean","COPY",FACE,{"derivedFrom":makeQuery(id+"F4.opRevolve","SWEPT_FACE",FACE,{"disambiguationData":[OSD([sQuery(id+"F2.wireOp",EDGE,"E16.rect.left")])]})})])],"derivedFrom":makeQuery(id+"F4.boolean.opBoolean","INTERSECT",EDGE,{"derivedFrom":[subQ0,subQ1]})});}
            var Q16;
            Q16=makeQuery(id+"F9.boolean.opBoolean","INTERSECT",EDGE,{"derivedFrom":[makeQuery(id+"F4.boolean.opBoolean","COPY",FACE,{"derivedFrom":makeQuery(id+"F4.opRevolve","SWEPT_FACE",FACE,{"disambiguationData":[OSD([sQuery(id+"F2.wireOp",EDGE,"E16.rect.bottom")])]})}),makeQuery(id+"F9.opRevolve","SWEPT_FACE",FACE,{"disambiguationData":[OSD([sQuery(id+"F6.wireOp",EDGE,"E23.rect.left")])]})]});
            var Q17;
            Q17=makeQuery(id+"F9.boolean.opBoolean","COPY",EDGE,{"derivedFrom":makeQuery(id+"F9.opRevolve","SWEPT_EDGE",EDGE,{"disambiguationData":[OSD([sQuery(id+"F6.wireOp",EDGE,"E23.rect.top"),sQuery(id+"F6.wireOp",EDGE,"E23.rect.left")])]})});
            var Q18;
            Q18=makeQuery(id+"F9.boolean.opBoolean","INTERSECT",EDGE,{"disambiguationData":[OD(0.0)],"derivedFrom":[makeQuery(id+"F1.opExtrude","CAP_FACE",FACE,{"disambiguationData":[OSD([sQuery(id+"F0.wireOp",EDGE,"E0.rect.bottom"),sQuery(id+"F0.wireOp",EDGE,"E0.rect.top"),sQuery(id+"F0.wireOp",EDGE,"E0.rect.left"),sQuery(id+"F0.wireOp",EDGE,"E0.rect.right")])],"isStart":true}),makeQuery(id+"F9.opRevolve","SWEPT_FACE",FACE,{"disambiguationData":[OSD([sQuery(id+"F6.wireOp",EDGE,"E23.rect.left")])]})]});
            var Q19;
            Q19=makeQuery(id+"F9.boolean.opBoolean","INTERSECT",EDGE,{"derivedFrom":[makeQuery(id+"F1.opExtrude","CAP_FACE",FACE,{"disambiguationData":[OSD([sQuery(id+"F0.wireOp",EDGE,"E0.rect.bottom"),sQuery(id+"F0.wireOp",EDGE,"E0.rect.top"),sQuery(id+"F0.wireOp",EDGE,"E0.rect.left"),sQuery(id+"F0.wireOp",EDGE,"E0.rect.right")])],"isStart":true}),makeQuery(id+"F9.opRevolve","SWEPT_FACE",FACE,{"disambiguationData":[OSD([sQuery(id+"F6.wireOp",EDGE,"E23.rect.top")])]})]});
            var Q20;
            Q20=makeQuery(id+"F4.boolean.opBoolean","COPY",EDGE,{"derivedFrom":makeQuery(id+"F4.opRevolve","SWEPT_EDGE",EDGE,{"disambiguationData":[OSD([sQuery(id+"F2.wireOp",EDGE,"E16.rect.bottom"),sQuery(id+"F2.wireOp",EDGE,"E16.rect.left")])]})});
            var Q21;
            Q21=makeQuery(id+"F9.boolean.opBoolean","INTERSECT",EDGE,{"disambiguationData":[OD(1.0)],"derivedFrom":[makeQuery(id+"F1.opExtrude","CAP_FACE",FACE,{"disambiguationData":[OSD([sQuery(id+"F0.wireOp",EDGE,"E0.rect.bottom"),sQuery(id+"F0.wireOp",EDGE,"E0.rect.top"),sQuery(id+"F0.wireOp",EDGE,"E0.rect.left"),sQuery(id+"F0.wireOp",EDGE,"E0.rect.right")])],"isStart":true}),makeQuery(id+"F9.opRevolve","SWEPT_FACE",FACE,{"disambiguationData":[OSD([sQuery(id+"F6.wireOp",EDGE,"E23.rect.left")])]})]});
            var Q22;
            {var subQ0=makeQuery(id+"F1.opExtrude","CAP_FACE",FACE,{"disambiguationData":[OSD([sQuery(id+"F0.wireOp",EDGE,"E0.rect.bottom"),sQuery(id+"F0.wireOp",EDGE,"E0.rect.top"),sQuery(id+"F0.wireOp",EDGE,"E0.rect.left"),sQuery(id+"F0.wireOp",EDGE,"E0.rect.right")])],"isStart":true});var subQ1=makeQuery(id+"F4.opRevolve","SWEPT_FACE",FACE,{"disambiguationData":[OSD([sQuery(id+"F2.wireOp",EDGE,"E16.rect.bottom")])]});Q22=makeQuery(id+"F9.boolean.opBoolean","SPLIT",EDGE,{"disambiguationData":[TD([makeQuery(id+"F8.boolean.opBoolean","COPY",FACE,{"derivedFrom":makeQuery(id+"F8.opRevolve","SWEPT_FACE",FACE,{"disambiguationData":[OSD([sQuery(id+"F6.wireOp",EDGE,"E22.rect.right")])]})})])],"derivedFrom":makeQuery(id+"F4.boolean.opBoolean","INTERSECT",EDGE,{"derivedFrom":[subQ0,subQ1]})});}
            var Q23;
            Q23=makeQuery(id+"F8.boolean.opBoolean","INTERSECT",EDGE,{"derivedFrom":[makeQuery(id+"F4.boolean.opBoolean","COPY",FACE,{"derivedFrom":makeQuery(id+"F4.opRevolve","SWEPT_FACE",FACE,{"disambiguationData":[OSD([sQuery(id+"F2.wireOp",EDGE,"E16.rect.bottom")])]})}),makeQuery(id+"F8.opRevolve","SWEPT_FACE",FACE,{"disambiguationData":[OSD([sQuery(id+"F6.wireOp",EDGE,"E22.rect.right")])]})]});
            var Q24;
            Q24=makeQuery(id+"F8.boolean.opBoolean","INTERSECT",EDGE,{"disambiguationData":[OD(0.0)],"derivedFrom":[makeQuery(id+"F1.opExtrude","CAP_FACE",FACE,{"disambiguationData":[OSD([sQuery(id+"F0.wireOp",EDGE,"E0.rect.bottom"),sQuery(id+"F0.wireOp",EDGE,"E0.rect.top"),sQuery(id+"F0.wireOp",EDGE,"E0.rect.left"),sQuery(id+"F0.wireOp",EDGE,"E0.rect.right")])],"isStart":true}),makeQuery(id+"F8.opRevolve","SWEPT_FACE",FACE,{"disambiguationData":[OSD([sQuery(id+"F6.wireOp",EDGE,"E22.rect.right")])]})]});
            var Q25;
            Q25=makeQuery(id+"F8.boolean.opBoolean","COPY",EDGE,{"derivedFrom":makeQuery(id+"F8.opRevolve","SWEPT_EDGE",EDGE,{"disambiguationData":[OSD([sQuery(id+"F6.wireOp",EDGE,"E22.rect.top"),sQuery(id+"F6.wireOp",EDGE,"E22.rect.right")])]})});
            var Q26;
            Q26=makeQuery(id+"F8.boolean.opBoolean","INTERSECT",EDGE,{"derivedFrom":[makeQuery(id+"F1.opExtrude","CAP_FACE",FACE,{"disambiguationData":[OSD([sQuery(id+"F0.wireOp",EDGE,"E0.rect.bottom"),sQuery(id+"F0.wireOp",EDGE,"E0.rect.top"),sQuery(id+"F0.wireOp",EDGE,"E0.rect.left"),sQuery(id+"F0.wireOp",EDGE,"E0.rect.right")])],"isStart":true}),makeQuery(id+"F8.opRevolve","SWEPT_FACE",FACE,{"disambiguationData":[OSD([sQuery(id+"F6.wireOp",EDGE,"E22.rect.top")])]})]});
            var Q27;
            Q27=makeQuery(id+"F3.boolean.opBoolean","COPY",EDGE,{"derivedFrom":makeQuery(id+"F3.opRevolve","SWEPT_EDGE",EDGE,{"disambiguationData":[OSD([sQuery(id+"F2.wireOp",EDGE,"E15.rect.bottom"),sQuery(id+"F2.wireOp",EDGE,"E15.rect.right")])]})});
            var Q28;
            Q28=makeQuery(id+"F8.boolean.opBoolean","INTERSECT",EDGE,{"derivedFrom":[makeQuery(id+"F4.boolean.opBoolean","COPY",FACE,{"derivedFrom":makeQuery(id+"F4.opRevolve","SWEPT_FACE",FACE,{"disambiguationData":[OSD([sQuery(id+"F2.wireOp",EDGE,"E16.rect.left")])]})}),makeQuery(id+"F8.opRevolve","SWEPT_FACE",FACE,{"disambiguationData":[OSD([sQuery(id+"F6.wireOp",EDGE,"E22.rect.right")])]})]});
            var Q29;
            Q29=makeQuery(id+"F8.boolean.opBoolean","INTERSECT",EDGE,{"derivedFrom":[makeQuery(id+"F3.boolean.opBoolean","COPY",FACE,{"derivedFrom":makeQuery(id+"F3.opRevolve","SWEPT_FACE",FACE,{"disambiguationData":[OSD([sQuery(id+"F2.wireOp",EDGE,"E15.rect.right")])]})}),makeQuery(id+"F8.opRevolve","SWEPT_FACE",FACE,{"disambiguationData":[OSD([sQuery(id+"F6.wireOp",EDGE,"E22.rect.right")])]})]});
            var Q30;
            Q30=makeQuery(id+"F8.boolean.opBoolean","INTERSECT",EDGE,{"derivedFrom":[makeQuery(id+"F3.boolean.opBoolean","COPY",FACE,{"derivedFrom":makeQuery(id+"F3.opRevolve","SWEPT_FACE",FACE,{"disambiguationData":[OSD([sQuery(id+"F2.wireOp",EDGE,"E15.rect.bottom")])]})}),makeQuery(id+"F8.opRevolve","SWEPT_FACE",FACE,{"disambiguationData":[OSD([sQuery(id+"F6.wireOp",EDGE,"E22.rect.right")])]})]});
            var Q31;
            Q31=makeQuery(id+"F3.boolean.opBoolean","INTERSECT",EDGE,{"derivedFrom":[makeQuery(id+"F1.opExtrude","CAP_FACE",FACE,{"disambiguationData":[OSD([sQuery(id+"F0.wireOp",EDGE,"E0.rect.bottom"),sQuery(id+"F0.wireOp",EDGE,"E0.rect.top"),sQuery(id+"F0.wireOp",EDGE,"E0.rect.left"),sQuery(id+"F0.wireOp",EDGE,"E0.rect.right")])],"isStart":true}),makeQuery(id+"F3.opRevolve","SWEPT_FACE",FACE,{"disambiguationData":[OSD([sQuery(id+"F2.wireOp",EDGE,"E15.rect.bottom")])]})]});
            var Q32;
            Q32=makeQuery(id+"F8.boolean.opBoolean","INTERSECT",EDGE,{"disambiguationData":[OD(2.0)],"derivedFrom":[makeQuery(id+"F1.opExtrude","CAP_FACE",FACE,{"disambiguationData":[OSD([sQuery(id+"F0.wireOp",EDGE,"E0.rect.bottom"),sQuery(id+"F0.wireOp",EDGE,"E0.rect.top"),sQuery(id+"F0.wireOp",EDGE,"E0.rect.left"),sQuery(id+"F0.wireOp",EDGE,"E0.rect.right")])],"isStart":true}),makeQuery(id+"F8.opRevolve","SWEPT_FACE",FACE,{"disambiguationData":[OSD([sQuery(id+"F6.wireOp",EDGE,"E22.rect.right")])]})]});
            var Q33;
            Q33=makeQuery(id+"F7.boolean.opBoolean","INTERSECT",EDGE,{"disambiguationData":[OD(0.0)],"derivedFrom":[makeQuery(id+"F1.opExtrude","CAP_FACE",FACE,{"disambiguationData":[OSD([sQuery(id+"F0.wireOp",EDGE,"E0.rect.bottom"),sQuery(id+"F0.wireOp",EDGE,"E0.rect.top"),sQuery(id+"F0.wireOp",EDGE,"E0.rect.left"),sQuery(id+"F0.wireOp",EDGE,"E0.rect.right")])],"isStart":true}),makeQuery(id+"F7.opRevolve","SWEPT_FACE",FACE,{"disambiguationData":[OSD([sQuery(id+"F6.wireOp",EDGE,"E21.rect.right")])]})]});
            var Q34;
            Q34=makeQuery(id+"F7.boolean.opBoolean","INTERSECT",EDGE,{"derivedFrom":[makeQuery(id+"F3.boolean.opBoolean","COPY",FACE,{"derivedFrom":makeQuery(id+"F3.opRevolve","SWEPT_FACE",FACE,{"disambiguationData":[OSD([sQuery(id+"F2.wireOp",EDGE,"E15.rect.bottom")])]})}),makeQuery(id+"F7.opRevolve","SWEPT_FACE",FACE,{"disambiguationData":[OSD([sQuery(id+"F6.wireOp",EDGE,"E21.rect.right")])]})]});
            var Q35;
            Q35=makeQuery(id+"F7.boolean.opBoolean","COPY",EDGE,{"derivedFrom":makeQuery(id+"F7.opRevolve","SWEPT_EDGE",EDGE,{"disambiguationData":[OSD([sQuery(id+"F6.wireOp",EDGE,"E21.rect.top"),sQuery(id+"F6.wireOp",EDGE,"E21.rect.right")])]})});
            var Q36;
            Q36=makeQuery(id+"F7.boolean.opBoolean","INTERSECT",EDGE,{"derivedFrom":[makeQuery(id+"F1.opExtrude","CAP_FACE",FACE,{"disambiguationData":[OSD([sQuery(id+"F0.wireOp",EDGE,"E0.rect.bottom"),sQuery(id+"F0.wireOp",EDGE,"E0.rect.top"),sQuery(id+"F0.wireOp",EDGE,"E0.rect.left"),sQuery(id+"F0.wireOp",EDGE,"E0.rect.right")])],"isStart":true}),makeQuery(id+"F7.opRevolve","SWEPT_FACE",FACE,{"disambiguationData":[OSD([sQuery(id+"F6.wireOp",EDGE,"E21.rect.top")])]})]});
            var Q37;
            Q37=makeQuery(id+"F7.boolean.opBoolean","INTERSECT",EDGE,{"disambiguationData":[OD(2.0)],"derivedFrom":[makeQuery(id+"F1.opExtrude","CAP_FACE",FACE,{"disambiguationData":[OSD([sQuery(id+"F0.wireOp",EDGE,"E0.rect.bottom"),sQuery(id+"F0.wireOp",EDGE,"E0.rect.top"),sQuery(id+"F0.wireOp",EDGE,"E0.rect.left"),sQuery(id+"F0.wireOp",EDGE,"E0.rect.right")])],"isStart":true}),makeQuery(id+"F7.opRevolve","SWEPT_FACE",FACE,{"disambiguationData":[OSD([sQuery(id+"F6.wireOp",EDGE,"E21.rect.right")])]})]});
            var Q38;
            Q38=makeQuery(id+"F7.boolean.opBoolean","INTERSECT",EDGE,{"derivedFrom":[makeQuery(id+"F3.boolean.opBoolean","COPY",FACE,{"derivedFrom":makeQuery(id+"F3.opRevolve","SWEPT_FACE",FACE,{"disambiguationData":[OSD([sQuery(id+"F2.wireOp",EDGE,"E15.rect.right")])]})}),makeQuery(id+"F7.opRevolve","SWEPT_FACE",FACE,{"disambiguationData":[OSD([sQuery(id+"F6.wireOp",EDGE,"E21.rect.right")])]})]});
            var Q39;
            Q39=makeQuery(id+"F7.boolean.opBoolean","INTERSECT",EDGE,{"derivedFrom":[makeQuery(id+"F1.opExtrude","CAP_FACE",FACE,{"disambiguationData":[OSD([sQuery(id+"F0.wireOp",EDGE,"E0.rect.bottom"),sQuery(id+"F0.wireOp",EDGE,"E0.rect.top"),sQuery(id+"F0.wireOp",EDGE,"E0.rect.left"),sQuery(id+"F0.wireOp",EDGE,"E0.rect.right")])],"isStart":true}),makeQuery(id+"F7.opRevolve","SWEPT_FACE",FACE,{"disambiguationData":[OSD([sQuery(id+"F6.wireOp",EDGE,"E21.rect.bottom")])]})]});
            var Q40;
            Q40=makeQuery(id+"F7.boolean.opBoolean","COPY",EDGE,{"derivedFrom":makeQuery(id+"F7.opRevolve","SWEPT_EDGE",EDGE,{"disambiguationData":[OSD([sQuery(id+"F6.wireOp",EDGE,"E21.rect.bottom"),sQuery(id+"F6.wireOp",EDGE,"E21.rect.right")])]})});
            var Q41;
            Q41=makeQuery(id+"F7.boolean.opBoolean","INTERSECT",EDGE,{"derivedFrom":[makeQuery(id+"F3.boolean.opBoolean","COPY",FACE,{"derivedFrom":makeQuery(id+"F3.opRevolve","SWEPT_FACE",FACE,{"disambiguationData":[OSD([sQuery(id+"F2.wireOp",EDGE,"E15.rect.top")])]})}),makeQuery(id+"F7.opRevolve","SWEPT_FACE",FACE,{"disambiguationData":[OSD([sQuery(id+"F6.wireOp",EDGE,"E21.rect.right")])]})]});
            var Q42;
            Q42=makeQuery(id+"F3.boolean.opBoolean","INTERSECT",EDGE,{"derivedFrom":[makeQuery(id+"F1.opExtrude","CAP_FACE",FACE,{"disambiguationData":[OSD([sQuery(id+"F0.wireOp",EDGE,"E0.rect.bottom"),sQuery(id+"F0.wireOp",EDGE,"E0.rect.top"),sQuery(id+"F0.wireOp",EDGE,"E0.rect.left"),sQuery(id+"F0.wireOp",EDGE,"E0.rect.right")])],"isStart":true}),makeQuery(id+"F3.opRevolve","SWEPT_FACE",FACE,{"disambiguationData":[OSD([sQuery(id+"F2.wireOp",EDGE,"E15.rect.top")])]})]});
            var Q43;
            Q43=makeQuery(id+"F7.boolean.opBoolean","INTERSECT",EDGE,{"disambiguationData":[OD(1.0)],"derivedFrom":[makeQuery(id+"F1.opExtrude","CAP_FACE",FACE,{"disambiguationData":[OSD([sQuery(id+"F0.wireOp",EDGE,"E0.rect.bottom"),sQuery(id+"F0.wireOp",EDGE,"E0.rect.top"),sQuery(id+"F0.wireOp",EDGE,"E0.rect.left"),sQuery(id+"F0.wireOp",EDGE,"E0.rect.right")])],"isStart":true}),makeQuery(id+"F7.opRevolve","SWEPT_FACE",FACE,{"disambiguationData":[OSD([sQuery(id+"F6.wireOp",EDGE,"E21.rect.right")])]})]});
            var Q44;
            Q44=makeQuery(id+"F8.boolean.opBoolean","INTERSECT",EDGE,{"disambiguationData":[OD(3.0)],"derivedFrom":[makeQuery(id+"F1.opExtrude","CAP_FACE",FACE,{"disambiguationData":[OSD([sQuery(id+"F0.wireOp",EDGE,"E0.rect.bottom"),sQuery(id+"F0.wireOp",EDGE,"E0.rect.top"),sQuery(id+"F0.wireOp",EDGE,"E0.rect.left"),sQuery(id+"F0.wireOp",EDGE,"E0.rect.right")])],"isStart":true}),makeQuery(id+"F8.opRevolve","SWEPT_FACE",FACE,{"disambiguationData":[OSD([sQuery(id+"F6.wireOp",EDGE,"E22.rect.right")])]})]});
            var Q45;
            Q45=makeQuery(id+"F8.boolean.opBoolean","INTERSECT",EDGE,{"derivedFrom":[makeQuery(id+"F1.opExtrude","CAP_FACE",FACE,{"disambiguationData":[OSD([sQuery(id+"F0.wireOp",EDGE,"E0.rect.bottom"),sQuery(id+"F0.wireOp",EDGE,"E0.rect.top"),sQuery(id+"F0.wireOp",EDGE,"E0.rect.left"),sQuery(id+"F0.wireOp",EDGE,"E0.rect.right")])],"isStart":true}),makeQuery(id+"F8.opRevolve","SWEPT_FACE",FACE,{"disambiguationData":[OSD([sQuery(id+"F6.wireOp",EDGE,"E22.rect.bottom")])]})]});
            var Q46;
            Q46=makeQuery(id+"F3.boolean.opBoolean","COPY",EDGE,{"derivedFrom":makeQuery(id+"F3.opRevolve","SWEPT_EDGE",EDGE,{"disambiguationData":[OSD([sQuery(id+"F2.wireOp",EDGE,"E15.rect.top"),sQuery(id+"F2.wireOp",EDGE,"E15.rect.right")])]})});
            var Q47;
            Q47=makeQuery(id+"F8.boolean.opBoolean","INTERSECT",EDGE,{"derivedFrom":[makeQuery(id+"F3.boolean.opBoolean","COPY",FACE,{"derivedFrom":makeQuery(id+"F3.opRevolve","SWEPT_FACE",FACE,{"disambiguationData":[OSD([sQuery(id+"F2.wireOp",EDGE,"E15.rect.top")])]})}),makeQuery(id+"F8.opRevolve","SWEPT_FACE",FACE,{"disambiguationData":[OSD([sQuery(id+"F6.wireOp",EDGE,"E22.rect.right")])]})]});
            var Q48;
            Q48=makeQuery(id+"F8.boolean.opBoolean","COPY",EDGE,{"derivedFrom":makeQuery(id+"F8.opRevolve","SWEPT_EDGE",EDGE,{"disambiguationData":[OSD([sQuery(id+"F6.wireOp",EDGE,"E22.rect.bottom"),sQuery(id+"F6.wireOp",EDGE,"E22.rect.right")])]})});
            var Q49;
            Q49=makeQuery(id+"F8.boolean.opBoolean","INTERSECT",EDGE,{"derivedFrom":[makeQuery(id+"F4.boolean.opBoolean","COPY",FACE,{"derivedFrom":makeQuery(id+"F4.opRevolve","SWEPT_FACE",FACE,{"disambiguationData":[OSD([sQuery(id+"F2.wireOp",EDGE,"E16.rect.top")])]})}),makeQuery(id+"F8.opRevolve","SWEPT_FACE",FACE,{"disambiguationData":[OSD([sQuery(id+"F6.wireOp",EDGE,"E22.rect.right")])]})]});
            var Q50;
            Q50=makeQuery(id+"F8.boolean.opBoolean","INTERSECT",EDGE,{"disambiguationData":[OD(1.0)],"derivedFrom":[makeQuery(id+"F1.opExtrude","CAP_FACE",FACE,{"disambiguationData":[OSD([sQuery(id+"F0.wireOp",EDGE,"E0.rect.bottom"),sQuery(id+"F0.wireOp",EDGE,"E0.rect.top"),sQuery(id+"F0.wireOp",EDGE,"E0.rect.left"),sQuery(id+"F0.wireOp",EDGE,"E0.rect.right")])],"isStart":true}),makeQuery(id+"F8.opRevolve","SWEPT_FACE",FACE,{"disambiguationData":[OSD([sQuery(id+"F6.wireOp",EDGE,"E22.rect.right")])]})]});
            var Q51;
            Q51=makeQuery(id+"F9.boolean.opBoolean","INTERSECT",EDGE,{"disambiguationData":[OD(3.0)],"derivedFrom":[makeQuery(id+"F1.opExtrude","CAP_FACE",FACE,{"disambiguationData":[OSD([sQuery(id+"F0.wireOp",EDGE,"E0.rect.bottom"),sQuery(id+"F0.wireOp",EDGE,"E0.rect.top"),sQuery(id+"F0.wireOp",EDGE,"E0.rect.left"),sQuery(id+"F0.wireOp",EDGE,"E0.rect.right")])],"isStart":true}),makeQuery(id+"F9.opRevolve","SWEPT_FACE",FACE,{"disambiguationData":[OSD([sQuery(id+"F6.wireOp",EDGE,"E23.rect.left")])]})]});
            var Q52;
            {var subQ0=makeQuery(id+"F1.opExtrude","CAP_FACE",FACE,{"disambiguationData":[OSD([sQuery(id+"F0.wireOp",EDGE,"E0.rect.bottom"),sQuery(id+"F0.wireOp",EDGE,"E0.rect.top"),sQuery(id+"F0.wireOp",EDGE,"E0.rect.left"),sQuery(id+"F0.wireOp",EDGE,"E0.rect.right")])],"isStart":true});var subQ1=makeQuery(id+"F4.opRevolve","SWEPT_FACE",FACE,{"disambiguationData":[OSD([sQuery(id+"F2.wireOp",EDGE,"E16.rect.top")])]});Q52=makeQuery(id+"F9.boolean.opBoolean","SPLIT",EDGE,{"disambiguationData":[TD([makeQuery(id+"F8.boolean.opBoolean","COPY",FACE,{"derivedFrom":makeQuery(id+"F8.opRevolve","SWEPT_FACE",FACE,{"disambiguationData":[OSD([sQuery(id+"F6.wireOp",EDGE,"E22.rect.right")])]})})])],"derivedFrom":makeQuery(id+"F4.boolean.opBoolean","INTERSECT",EDGE,{"derivedFrom":[subQ0,subQ1]})});}
            var Q53;
            Q53=makeQuery(id+"F4.boolean.opBoolean","COPY",EDGE,{"derivedFrom":makeQuery(id+"F4.opRevolve","SWEPT_EDGE",EDGE,{"disambiguationData":[OSD([sQuery(id+"F2.wireOp",EDGE,"E16.rect.top"),sQuery(id+"F2.wireOp",EDGE,"E16.rect.left")])]})});
            var Q54;
            Q54=makeQuery(id+"F9.boolean.opBoolean","INTERSECT",EDGE,{"derivedFrom":[makeQuery(id+"F4.boolean.opBoolean","COPY",FACE,{"derivedFrom":makeQuery(id+"F4.opRevolve","SWEPT_FACE",FACE,{"disambiguationData":[OSD([sQuery(id+"F2.wireOp",EDGE,"E16.rect.top")])]})}),makeQuery(id+"F9.opRevolve","SWEPT_FACE",FACE,{"disambiguationData":[OSD([sQuery(id+"F6.wireOp",EDGE,"E23.rect.left")])]})]});
            var Q55;
            Q55=makeQuery(id+"F9.boolean.opBoolean","COPY",EDGE,{"derivedFrom":makeQuery(id+"F9.opRevolve","SWEPT_EDGE",EDGE,{"disambiguationData":[OSD([sQuery(id+"F6.wireOp",EDGE,"E23.rect.bottom"),sQuery(id+"F6.wireOp",EDGE,"E23.rect.left")])]})});
            var Q56;
            Q56=makeQuery(id+"F9.boolean.opBoolean","INTERSECT",EDGE,{"derivedFrom":[makeQuery(id+"F1.opExtrude","CAP_FACE",FACE,{"disambiguationData":[OSD([sQuery(id+"F0.wireOp",EDGE,"E0.rect.bottom"),sQuery(id+"F0.wireOp",EDGE,"E0.rect.top"),sQuery(id+"F0.wireOp",EDGE,"E0.rect.left"),sQuery(id+"F0.wireOp",EDGE,"E0.rect.right")])],"isStart":true}),makeQuery(id+"F9.opRevolve","SWEPT_FACE",FACE,{"disambiguationData":[OSD([sQuery(id+"F6.wireOp",EDGE,"E23.rect.bottom")])]})]});
            var Q57;
            Q57=makeQuery(id+"F9.boolean.opBoolean","INTERSECT",EDGE,{"disambiguationData":[OD(2.0)],"derivedFrom":[makeQuery(id+"F1.opExtrude","CAP_FACE",FACE,{"disambiguationData":[OSD([sQuery(id+"F0.wireOp",EDGE,"E0.rect.bottom"),sQuery(id+"F0.wireOp",EDGE,"E0.rect.top"),sQuery(id+"F0.wireOp",EDGE,"E0.rect.left"),sQuery(id+"F0.wireOp",EDGE,"E0.rect.right")])],"isStart":true}),makeQuery(id+"F9.opRevolve","SWEPT_FACE",FACE,{"disambiguationData":[OSD([sQuery(id+"F6.wireOp",EDGE,"E23.rect.left")])]})]});
            var Q58;
            {var subQ0=makeQuery(id+"F1.opExtrude","CAP_FACE",FACE,{"disambiguationData":[OSD([sQuery(id+"F0.wireOp",EDGE,"E0.rect.bottom"),sQuery(id+"F0.wireOp",EDGE,"E0.rect.top"),sQuery(id+"F0.wireOp",EDGE,"E0.rect.left"),sQuery(id+"F0.wireOp",EDGE,"E0.rect.right")])],"isStart":true});var subQ1=makeQuery(id+"F4.opRevolve","SWEPT_FACE",FACE,{"disambiguationData":[OSD([sQuery(id+"F2.wireOp",EDGE,"E16.rect.top")])]});Q58=makeQuery(id+"F9.boolean.opBoolean","SPLIT",EDGE,{"disambiguationData":[TD([makeQuery(id+"F4.boolean.opBoolean","COPY",FACE,{"derivedFrom":makeQuery(id+"F4.opRevolve","SWEPT_FACE",FACE,{"disambiguationData":[OSD([sQuery(id+"F2.wireOp",EDGE,"E16.rect.left")])]})})])],"derivedFrom":makeQuery(id+"F4.boolean.opBoolean","INTERSECT",EDGE,{"derivedFrom":[subQ0,subQ1]})});}
            var Q59;
            Q59=makeQuery(id+"F10.boolean.opBoolean","INTERSECT",EDGE,{"disambiguationData":[OD(3.0)],"derivedFrom":[makeQuery(id+"F1.opExtrude","CAP_FACE",FACE,{"disambiguationData":[OSD([sQuery(id+"F0.wireOp",EDGE,"E0.rect.bottom"),sQuery(id+"F0.wireOp",EDGE,"E0.rect.top"),sQuery(id+"F0.wireOp",EDGE,"E0.rect.left"),sQuery(id+"F0.wireOp",EDGE,"E0.rect.right")])],"isStart":true}),makeQuery(id+"F10.opRevolve","SWEPT_FACE",FACE,{"disambiguationData":[OSD([sQuery(id+"F6.wireOp",EDGE,"E24.rect.right")])]})]});
            var Q60;
            Q60=makeQuery(id+"F10.boolean.opBoolean","INTERSECT",EDGE,{"derivedFrom":[makeQuery(id+"F4.boolean.opBoolean","COPY",FACE,{"derivedFrom":makeQuery(id+"F4.opRevolve","SWEPT_FACE",FACE,{"disambiguationData":[OSD([sQuery(id+"F2.wireOp",EDGE,"E16.rect.top")])]})}),makeQuery(id+"F10.opRevolve","SWEPT_FACE",FACE,{"disambiguationData":[OSD([sQuery(id+"F6.wireOp",EDGE,"E24.rect.right")])]})]});
            var Q61;
            Q61=makeQuery(id+"F10.boolean.opBoolean","COPY",EDGE,{"derivedFrom":makeQuery(id+"F10.opRevolve","SWEPT_EDGE",EDGE,{"disambiguationData":[OSD([sQuery(id+"F6.wireOp",EDGE,"E24.rect.bottom"),sQuery(id+"F6.wireOp",EDGE,"E24.rect.right")])]})});
            var Q62;
            Q62=makeQuery(id+"F10.boolean.opBoolean","INTERSECT",EDGE,{"derivedFrom":[makeQuery(id+"F1.opExtrude","CAP_FACE",FACE,{"disambiguationData":[OSD([sQuery(id+"F0.wireOp",EDGE,"E0.rect.bottom"),sQuery(id+"F0.wireOp",EDGE,"E0.rect.top"),sQuery(id+"F0.wireOp",EDGE,"E0.rect.left"),sQuery(id+"F0.wireOp",EDGE,"E0.rect.right")])],"isStart":true}),makeQuery(id+"F10.opRevolve","SWEPT_FACE",FACE,{"disambiguationData":[OSD([sQuery(id+"F6.wireOp",EDGE,"E24.rect.bottom")])]})]});
            var Q63;
            Q63=makeQuery(id+"F10.boolean.opBoolean","INTERSECT",EDGE,{"disambiguationData":[OD(0.0)],"derivedFrom":[makeQuery(id+"F1.opExtrude","CAP_FACE",FACE,{"disambiguationData":[OSD([sQuery(id+"F0.wireOp",EDGE,"E0.rect.bottom"),sQuery(id+"F0.wireOp",EDGE,"E0.rect.top"),sQuery(id+"F0.wireOp",EDGE,"E0.rect.left"),sQuery(id+"F0.wireOp",EDGE,"E0.rect.right")])],"isStart":true}),makeQuery(id+"F10.opRevolve","SWEPT_FACE",FACE,{"disambiguationData":[OSD([sQuery(id+"F6.wireOp",EDGE,"E24.rect.right")])]})]});
            var Q64;
            Q64=makeQuery(id+"F5.boolean.opBoolean","INTERSECT",EDGE,{"derivedFrom":[makeQuery(id+"F1.opExtrude","CAP_FACE",FACE,{"disambiguationData":[OSD([sQuery(id+"F0.wireOp",EDGE,"E0.rect.bottom"),sQuery(id+"F0.wireOp",EDGE,"E0.rect.top"),sQuery(id+"F0.wireOp",EDGE,"E0.rect.left"),sQuery(id+"F0.wireOp",EDGE,"E0.rect.right")])],"isStart":true}),makeQuery(id+"F5.opRevolve","SWEPT_FACE",FACE,{"disambiguationData":[OSD([sQuery(id+"F2.wireOp",EDGE,"E17.rect.bottom")])]})]});
            var Q65;
            Q65=makeQuery(id+"F11.boolean.opBoolean","INTERSECT",EDGE,{"disambiguationData":[OD(0.0)],"derivedFrom":[makeQuery(id+"F1.opExtrude","CAP_FACE",FACE,{"disambiguationData":[OSD([sQuery(id+"F0.wireOp",EDGE,"E0.rect.bottom"),sQuery(id+"F0.wireOp",EDGE,"E0.rect.top"),sQuery(id+"F0.wireOp",EDGE,"E0.rect.left"),sQuery(id+"F0.wireOp",EDGE,"E0.rect.right")])],"isStart":true}),makeQuery(id+"F11.opRevolve","SWEPT_FACE",FACE,{"disambiguationData":[OSD([sQuery(id+"F6.wireOp",EDGE,"E25.rect.right")])]})]});
            var Q66;
            Q66=makeQuery(id+"F11.boolean.opBoolean","INTERSECT",EDGE,{"derivedFrom":[makeQuery(id+"F1.opExtrude","CAP_FACE",FACE,{"disambiguationData":[OSD([sQuery(id+"F0.wireOp",EDGE,"E0.rect.bottom"),sQuery(id+"F0.wireOp",EDGE,"E0.rect.top"),sQuery(id+"F0.wireOp",EDGE,"E0.rect.left"),sQuery(id+"F0.wireOp",EDGE,"E0.rect.right")])],"isStart":true}),makeQuery(id+"F11.opRevolve","SWEPT_FACE",FACE,{"disambiguationData":[OSD([sQuery(id+"F6.wireOp",EDGE,"E25.rect.bottom")])]})]});
            var Q67;
            Q67=makeQuery(id+"F11.boolean.opBoolean","INTERSECT",EDGE,{"derivedFrom":[makeQuery(id+"F5.boolean.opBoolean","COPY",FACE,{"derivedFrom":makeQuery(id+"F5.opRevolve","SWEPT_FACE",FACE,{"disambiguationData":[OSD([sQuery(id+"F2.wireOp",EDGE,"E17.rect.bottom")])]})}),makeQuery(id+"F11.opRevolve","SWEPT_FACE",FACE,{"disambiguationData":[OSD([sQuery(id+"F6.wireOp",EDGE,"E25.rect.right")])]})]});
            var Q68;
            Q68=makeQuery(id+"F11.boolean.opBoolean","COPY",EDGE,{"derivedFrom":makeQuery(id+"F11.opRevolve","SWEPT_EDGE",EDGE,{"disambiguationData":[OSD([sQuery(id+"F6.wireOp",EDGE,"E25.rect.bottom"),sQuery(id+"F6.wireOp",EDGE,"E25.rect.right")])]})});
            var Q69;
            Q69=makeQuery(id+"F5.boolean.opBoolean","COPY",EDGE,{"derivedFrom":makeQuery(id+"F5.opRevolve","SWEPT_EDGE",EDGE,{"disambiguationData":[OSD([sQuery(id+"F2.wireOp",EDGE,"E17.rect.bottom"),sQuery(id+"F2.wireOp",EDGE,"E17.rect.right")])]})});
            var Q70;
            Q70=makeQuery(id+"F10.boolean.opBoolean","INTERSECT",EDGE,{"derivedFrom":[makeQuery(id+"F5.boolean.opBoolean","COPY",FACE,{"derivedFrom":makeQuery(id+"F5.opRevolve","SWEPT_FACE",FACE,{"disambiguationData":[OSD([sQuery(id+"F2.wireOp",EDGE,"E17.rect.bottom")])]})}),makeQuery(id+"F10.opRevolve","SWEPT_FACE",FACE,{"disambiguationData":[OSD([sQuery(id+"F6.wireOp",EDGE,"E24.rect.right")])]})]});
            fillet(context, id + "F12", {"entities" : qUnion([Q0, Q1, Q2, Q3, Q4, Q5, Q6, Q7, Q8, Q9, Q10, Q11, Q12, Q13, Q14, Q15, Q16, Q17, Q18, Q19, Q20, Q21, Q22, Q23, Q24, Q25, Q26, Q27, Q28, Q29, Q30, Q31, Q32, Q33, Q34, Q35, Q36, Q37, Q38, Q39, Q40, Q41, Q42, Q43, Q44, Q45, Q46, Q47, Q48, Q49, Q50, Q51, Q52, Q53, Q54, Q55, Q56, Q57, Q58, Q59, Q60, Q61, Q62, Q63, Q64, Q65, Q66, Q67, Q68, Q69, Q70]), "radius" : 1 * mm, "tangentPropagation" : true, "rho" : 0.7, "crossSection" : FilletCrossSection.CONIC, "allowEdgeOverflow" : false});
        }
        {
            var Q0;
            Q0=makeQuery(id+"F1.opExtrude","CAP_EDGE",EDGE,{"disambiguationData":[OSD([sQuery(id+"F0.wireOp",EDGE,"E0.rect.bottom")])],"isStart":true});
            var Q1;
            Q1=makeQuery(id+"F1.opExtrude","SWEPT_EDGE",EDGE,{"disambiguationData":[OSD([sQuery(id+"F0.wireOp",EDGE,"E0.rect.bottom"),sQuery(id+"F0.wireOp",EDGE,"E0.rect.right")])]});
            var Q2;
            Q2=makeQuery(id+"F1.opExtrude","CAP_EDGE",EDGE,{"disambiguationData":[OSD([sQuery(id+"F0.wireOp",EDGE,"E0.rect.right")])],"isStart":true});
            var Q3;
            Q3=makeQuery(id+"F1.opExtrude","SWEPT_EDGE",EDGE,{"disambiguationData":[OSD([sQuery(id+"F0.wireOp",EDGE,"E0.rect.top"),sQuery(id+"F0.wireOp",EDGE,"E0.rect.right")])]});
            var Q4;
            Q4=makeQuery(id+"F1.opExtrude","CAP_EDGE",EDGE,{"disambiguationData":[OSD([sQuery(id+"F0.wireOp",EDGE,"E0.rect.top")])],"isStart":true});
            var Q5;
            Q5=makeQuery(id+"F1.opExtrude","SWEPT_EDGE",EDGE,{"disambiguationData":[OSD([sQuery(id+"F0.wireOp",EDGE,"E0.rect.top"),sQuery(id+"F0.wireOp",EDGE,"E0.rect.left")])]});
            var Q6;
            Q6=makeQuery(id+"F1.opExtrude","CAP_EDGE",EDGE,{"disambiguationData":[OSD([sQuery(id+"F0.wireOp",EDGE,"E0.rect.left")])],"isStart":true});
            var Q7;
            Q7=makeQuery(id+"F1.opExtrude","SWEPT_EDGE",EDGE,{"disambiguationData":[OSD([sQuery(id+"F0.wireOp",EDGE,"E0.rect.bottom"),sQuery(id+"F0.wireOp",EDGE,"E0.rect.left")])]});
            fillet(context, id + "F13", {"entities" : qUnion([Q0, Q1, Q2, Q3, Q4, Q5, Q6, Q7]), "radius" : 4 * mm, "tangentPropagation" : true, "rho" : 0.74, "crossSection" : FilletCrossSection.CONIC, "allowEdgeOverflow" : false});
        }
        {
            var Q0;
            Q0=makeQuery(id+"F13.opFillet","SPLIT",FACE,{"disambiguationData":[OD(1.0)],"derivedFrom":makeQuery(id+"F1.opExtrude","CAP_FACE",FACE,{"disambiguationData":[OSD([sQuery(id+"F0.wireOp",EDGE,"E0.rect.bottom"),sQuery(id+"F0.wireOp",EDGE,"E0.rect.top"),sQuery(id+"F0.wireOp",EDGE,"E0.rect.left"),sQuery(id+"F0.wireOp",EDGE,"E0.rect.right")])],"isStart":true})});
            var sketch = newSketch(context, id + "F14", { "sketchPlane" : qUnion([Q0])});
            skText(sketch, "E31", { "text": "ZuZ", "fontName": "NotoSans-Regular.ttf"});
            skPoint(sketch, "E32", {"position": v(0, -40) * mm});
            const initialGuessF14  = {"E31": [-0.00567, -0.04, 1, 0, 0.00473]};
            skSetInitialGuess(sketch, initialGuessF14);
            skSolve(sketch);
        }
        {
            var Q0;
            {var subQ21=sQuery(id+"F14.wireOp",EDGE,"E31.sketch_text.stroke-1");Q0=makeQuery(id+"F14.imprint","IMPRINT",FACE,{"disambiguationData":[TD([[makeQuery(id+"F14.imprint","IMPRINT",EDGE,{"derivedFrom":subQ21}),1.0]])]});}
            var sketch = newSketch(context, id + "F15", { "sketchPlane" : qUnion([Q0])});
            skLineSegment(sketch, "E33", {"start": v(-2.57, -35.3) * mm, "end": v(-5.41, -39.55) * mm});
            skLineSegment(sketch, "E34", {"start": v(-5.41, -39.55) * mm, "end": v(-5.41, -40) * mm});
            skLineSegment(sketch, "E35", {"start": v(-5.41, -40) * mm, "end": v(-2.16, -40) * mm});
            skLineSegment(sketch, "E36", {"start": v(-2.16, -40) * mm, "end": v(-2.16, -39.46) * mm});
            skLineSegment(sketch, "E37", {"start": v(-2.16, -39.46) * mm, "end": v(-4.7, -39.46) * mm});
            skLineSegment(sketch, "E38", {"start": v(-4.7, -39.46) * mm, "end": v(-1.92, -35.3) * mm});
            skLineSegment(sketch, "E39", {"start": v(-1.92, -35.3) * mm, "end": v(-2.57, -35.3) * mm});
            skLineSegment(sketch, "E40", {"start": v(-1.39, -38.83) * mm, "end": v(-1.39, -36.47) * mm});
            skLineSegment(sketch, "E41", {"start": v(-1.39, -36.47) * mm, "end": v(-0.8, -36.47) * mm});
            skLineSegment(sketch, "E42", {"start": v(-0.8, -36.47) * mm, "end": v(-0.8, -38.73) * mm});
            skLineSegment(sketch, "E43", {"start": v(1.03, -38.37) * mm, "end": v(1.03, -36.47) * mm});
            skLineSegment(sketch, "E44", {"start": v(1.03, -36.47) * mm, "end": v(1.6, -36.47) * mm});
            skLineSegment(sketch, "E45", {"start": v(1.6, -36.47) * mm, "end": v(1.6, -40) * mm});
            skLineSegment(sketch, "E46", {"start": v(1.6, -40) * mm, "end": v(1.13, -40) * mm});
            skLineSegment(sketch, "E47", {"start": v(1.13, -40) * mm, "end": v(1.04, -39.53) * mm});
            skLineSegment(sketch, "E48", {"start": v(1.04, -39.53) * mm, "end": v(1.01, -39.53) * mm});
            skPoint(sketch, "E49", {"position": v(-0.8, -38.73) * mm});
            skPoint(sketch, "E50.orphan", {"position": v(-0.8, -38.83) * mm});
            skFitSpline(sketch, "E51", {"points": [v(-0.8, -38.73) * mm, v(-0.76, -39.09) * mm, v(-0.68, -39.28) * mm, v(-0.56, -39.43) * mm, v(-0.4, -39.52) * mm, v(-0.18, -39.58) * mm, v(0, -39.59) * mm, v(0.25, -39.56) * mm, v(0.5, -39.49) * mm, v(0.7, -39.35) * mm, v(0.86, -39.15) * mm, v(0.96, -38.88) * mm, v(1, -38.63) * mm, v(1.03, -38.37) * mm], "startDerivative": vector(0.4, -4.05) * mm, "endDerivative": vector(0.2, 3.3) * mm});
            skArc(sketch, "E52.filletArc", {"start": v(-0.8, -38.73) * mm, "mid": v(-0.8, -38.73) * mm, "end": v(-0.8, -38.74) * mm});
            skFitSpline(sketch, "E53", {"points": [v(-1.39, -38.83) * mm, v(-1.34, -39.25) * mm, v(-1.26, -39.48) * mm, v(-1.17, -39.64) * mm, v(-1.03, -39.8) * mm, v(-0.85, -39.9) * mm, v(-0.68, -39.98) * mm, v(-0.46, -40.04) * mm, v(-0.19, -40.06) * mm, v(0, -40.06) * mm, v(0.2, -40.04) * mm, v(0.36, -40) * mm, v(0.5, -39.95) * mm, v(0.7, -39.86) * mm, v(0.85, -39.74) * mm, v(0.95, -39.63) * mm, v(1.01, -39.53) * mm], "startDerivative": vector(0.46, -5.04) * mm, "endDerivative": vector(1.39, 1.95) * mm});
            skLineSegment(sketch, "E54", {"start": v(2.49, -35.83) * mm, "end": v(2.49, -35.3) * mm, "construction": true});
            skLineSegment(sketch, "E55", {"start": v(2.49, -35.3) * mm, "end": v(5.6, -35.3) * mm, "construction": true});
            skLineSegment(sketch, "E56", {"start": v(5.6, -35.3) * mm, "end": v(5.6, -35.75) * mm, "construction": true});
            skLineSegment(sketch, "E57", {"start": v(5.6, -35.75) * mm, "end": v(3.12, -39.47) * mm, "construction": true});
            skLineSegment(sketch, "E58", {"start": v(3.12, -39.47) * mm, "end": v(5.66, -39.47) * mm, "construction": true});
            skLineSegment(sketch, "E59", {"start": v(5.66, -39.47) * mm, "end": v(5.66, -40) * mm, "construction": true});
            skLineSegment(sketch, "E60", {"start": v(5.66, -40) * mm, "end": v(2.42, -40) * mm, "construction": true});
            skLineSegment(sketch, "E61", {"start": v(2.42, -40) * mm, "end": v(2.42, -39.56) * mm, "construction": true});
            skLineSegment(sketch, "E62", {"start": v(2.42, -39.56) * mm, "end": v(4.89, -35.83) * mm, "construction": true});
            skLineSegment(sketch, "E63", {"start": v(2.49, -35.83) * mm, "end": v(4.89, -35.83) * mm, "construction": true});
            skText(sketch, "E64", { "text": "z", "fontName": "OpenSans-Regular.ttf"});
            const initialGuessF15  = {"E64": [0.00218, -0.04, 1, 0, 0.00475]};
            skSetInitialGuess(sketch, initialGuessF15);
            skSolve(sketch);
        }
        {
            var Q0;
            Q0=makeQuery(id+"F1.opExtrude","CAP_FACE",FACE,{"disambiguationData":[OSD([sQuery(id+"F0.wireOp",EDGE,"E0.rect.bottom"),sQuery(id+"F0.wireOp",EDGE,"E0.rect.top"),sQuery(id+"F0.wireOp",EDGE,"E0.rect.left"),sQuery(id+"F0.wireOp",EDGE,"E0.rect.right")])],"isStart":false});
            var sketch = newSketch(context, id + "F16", { "sketchPlane" : qUnion([Q0])});
            skLineSegment(sketch, "E65.rect.bottom", {"start": v(45, -45) * mm, "end": v(-45, -45) * mm});
            skLineSegment(sketch, "E65.rect.top", {"start": v(45, 45) * mm, "end": v(-45, 45) * mm});
            skLineSegment(sketch, "E65.rect.left", {"start": v(45, -45) * mm, "end": v(45, 45) * mm});
            skLineSegment(sketch, "E65.rect.right", {"start": v(-45, -45) * mm, "end": v(-45, 45) * mm});
            skPoint(sketch, "E65.rect.middle", {"position": v(0, 0) * mm});
            skLineSegment(sketch, "E66.rect.bottom", {"start": v(-49, 49) * mm, "end": v(143, 49) * mm});
            skLineSegment(sketch, "E66.rect.top", {"start": v(-49, -49) * mm, "end": v(143, -49) * mm});
            skLineSegment(sketch, "E66.rect.left", {"start": v(-49, 49) * mm, "end": v(-49, -49) * mm});
            skLineSegment(sketch, "E66.rect.right", {"start": v(143, 49) * mm, "end": v(143, -49) * mm});
            skPoint(sketch, "E66.rect.middle", {"position": v(47, 0) * mm});
            skLineSegment(sketch, "E67", {"start": v(47, 49) * mm, "end": v(47, -49) * mm, "construction": true});
            skLineSegment(sketch, "E68.MirrorCS", {"start": v(49, -45) * mm, "end": v(49, 45) * mm});
            skLineSegment(sketch, "E69.MirrorCS", {"start": v(49, 45) * mm, "end": v(139, 45) * mm});
            skLineSegment(sketch, "E70.MirrorCS", {"start": v(139, -45) * mm, "end": v(139, 45) * mm});
            skLineSegment(sketch, "E71.MirrorCS", {"start": v(49, -45) * mm, "end": v(139, -45) * mm});
            skLineSegment(sketch, "E72.rect.bottom", {"start": v(143, -49) * mm, "end": v(180, -49) * mm});
            skLineSegment(sketch, "E72.rect.top", {"start": v(143, 49) * mm, "end": v(180, 49) * mm});
            skLineSegment(sketch, "E72.rect.left", {"start": v(143, -49) * mm, "end": v(143, 49) * mm});
            skLineSegment(sketch, "E72.rect.right", {"start": v(180, -49) * mm, "end": v(180, 49) * mm});
            skPoint(sketch, "E72.rect.middle", {"position": v(161.5, 0) * mm});
            skCircle(sketch, "E73", {"center": v(161.5, -30.5) * mm, "radius": 12 * mm});
            skCircle(sketch, "E74", {"center": v(161.5, 0) * mm, "radius": 12 * mm});
            skCircle(sketch, "E75", {"center": v(161.5, 30.5) * mm, "radius": 12 * mm});
            skLineSegment(sketch, "E76", {"start": v(161.5, 42.5) * mm, "end": v(161.5, 49) * mm, "construction": true});
            skLineSegment(sketch, "E77", {"start": v(161.5, 18.5) * mm, "end": v(161.5, 12) * mm, "construction": true});
            skLineSegment(sketch, "E78", {"start": v(161.5, -12) * mm, "end": v(161.5, -18.5) * mm, "construction": true});
            skLineSegment(sketch, "E79", {"start": v(161.5, -42.5) * mm, "end": v(161.5, -49) * mm, "construction": true});
            skLineSegment(sketch, "E80", {"start": v(173.5, 0) * mm, "end": v(180, 0) * mm, "construction": true});
            skCircle(sketch, "E81", {"center": v(161.5, 30.5) * mm, "radius": 2 * mm});
            skCircle(sketch, "E82", {"center": v(161.5, 0) * mm, "radius": 2 * mm});
            skCircle(sketch, "E83", {"center": v(161.5, -30.5) * mm, "radius": 2 * mm});
            skSolve(sketch);
        }
        {
            var Q0;
            Q0=makeQuery(id+"F16.imprint","IMPRINT",FACE,{"disambiguationData":[TD([[makeQuery(id+"F16.imprint","IMPRINT",EDGE,{"derivedFrom":sQuery(id+"F16.wireOp",EDGE,"E68.MirrorCS")}),-1.0]])]});
            var Q1;
            {var subQ3=sQuery(id+"F0.wireOp",EDGE,"E0.rect.bottom");Q1=makeQuery(id+"F16.imprint","IMPRINT",FACE,{"disambiguationData":[TD([[makeQuery(id+"F16.imprint","IMPRINT",EDGE,{"derivedFrom":makeQuery(id+"F1.opExtrude","CAP_EDGE",EDGE,{"disambiguationData":[OSD([subQ3])],"isStart":false})}),-1.0]])]});}
            var Q2;
            Q2=makeQuery(id+"F16.imprint","IMPRINT",FACE,{"disambiguationData":[TD([[makeQuery(id+"F16.imprint","IMPRINT",EDGE,{"derivedFrom":sQuery(id+"F16.wireOp",EDGE,"E65.rect.bottom")}),-1.0]])]});
            var Q3;
            Q3=makeQuery(id+"F16.imprint","IMPRINT",FACE,{"disambiguationData":[TD([[makeQuery(id+"F16.imprint","IMPRINT",EDGE,{"derivedFrom":sQuery(id+"F16.wireOp",EDGE,"E83")}),1.0]])]});
            var Q4;
            Q4=makeQuery(id+"F16.imprint","IMPRINT",FACE,{"disambiguationData":[TD([[makeQuery(id+"F16.imprint","IMPRINT",EDGE,{"derivedFrom":sQuery(id+"F16.wireOp",EDGE,"E73")}),1.0]])]});
            var Q5;
            Q5=makeQuery(id+"F16.imprint","IMPRINT",FACE,{"disambiguationData":[TD([[makeQuery(id+"F16.imprint","IMPRINT",EDGE,{"derivedFrom":sQuery(id+"F16.wireOp",EDGE,"E82")}),1.0]])]});
            var Q6;
            Q6=makeQuery(id+"F16.imprint","IMPRINT",FACE,{"disambiguationData":[TD([[makeQuery(id+"F16.imprint","IMPRINT",EDGE,{"derivedFrom":sQuery(id+"F16.wireOp",EDGE,"E74")}),1.0]])]});
            var Q7;
            Q7=makeQuery(id+"F16.imprint","IMPRINT",FACE,{"disambiguationData":[TD([[makeQuery(id+"F16.imprint","IMPRINT",EDGE,{"derivedFrom":sQuery(id+"F16.wireOp",EDGE,"E72.rect.bottom")}),1.0]])]});
            var Q8;
            Q8=makeQuery(id+"F16.imprint","IMPRINT",FACE,{"disambiguationData":[TD([[makeQuery(id+"F16.imprint","IMPRINT",EDGE,{"derivedFrom":sQuery(id+"F16.wireOp",EDGE,"E81")}),1.0]])]});
            var Q9;
            Q9=makeQuery(id+"F16.imprint","IMPRINT",FACE,{"disambiguationData":[TD([[makeQuery(id+"F16.imprint","IMPRINT",EDGE,{"derivedFrom":sQuery(id+"F16.wireOp",EDGE,"E75")}),1.0]])]});
            var Q10;
            Q10=makeQuery(id+"F16.imprint","IMPRINT",FACE,{"disambiguationData":[TD([[makeQuery(id+"F16.imprint","IMPRINT",EDGE,{"derivedFrom":sQuery(id+"F16.wireOp",EDGE,"E65.rect.bottom")}),1.0]])]});
            extrude(context, id + "F17", {"entities" : qUnion([Q0, Q1, Q2, Q3, Q4, Q5, Q6, Q7, Q8, Q9, Q10]), "depth" : 5 * mm});
        }
        {
            var Q0;
            Q0=makeQuery(id+"F16.imprint","IMPRINT",FACE,{"disambiguationData":[TD([[makeQuery(id+"F16.imprint","IMPRINT",EDGE,{"derivedFrom":sQuery(id+"F16.wireOp",EDGE,"E65.rect.bottom")}),1.0]])]});
            var Q1;
            Q1=makeQuery(id+"F16.imprint","IMPRINT",FACE,{"disambiguationData":[TD([[makeQuery(id+"F16.imprint","IMPRINT",EDGE,{"derivedFrom":sQuery(id+"F16.wireOp",EDGE,"E72.rect.bottom")}),1.0]])]});
            var Q2;
            Q2=makeQuery(id+"F16.imprint","IMPRINT",FACE,{"disambiguationData":[TD([[makeQuery(id+"F16.imprint","IMPRINT",EDGE,{"derivedFrom":sQuery(id+"F16.wireOp",EDGE,"E83")}),1.0]])]});
            var Q3;
            Q3=makeQuery(id+"F16.imprint","IMPRINT",FACE,{"disambiguationData":[TD([[makeQuery(id+"F16.imprint","IMPRINT",EDGE,{"derivedFrom":sQuery(id+"F16.wireOp",EDGE,"E81")}),1.0]])]});
            var Q4;
            Q4=makeQuery(id+"F16.imprint","IMPRINT",FACE,{"disambiguationData":[TD([[makeQuery(id+"F16.imprint","IMPRINT",EDGE,{"derivedFrom":sQuery(id+"F16.wireOp",EDGE,"E82")}),1.0]])]});
            extrude(context, id + "F18", {"entities" : qUnion([Q0, Q1, Q2, Q3, Q4]), "operationType" : NewBodyOperationType.ADD, "oppositeDirection" : true, "depth" : 14 * mm});
        }
        {
            var Q0;
            {var subQ0=sQuery(id+"F16.wireOp",EDGE,"E66.rect.bottom");var subQ1=sQuery(id+"F16.wireOp",EDGE,"E66.rect.right");Q0=makeQuery(id+"F18.boolean.opBoolean","MERGE",EDGE,{"derivedFrom":[makeQuery(id+"F17.opExtrude","SWEPT_EDGE",EDGE,{"disambiguationData":[OSD([subQ0,subQ1])]}),makeQuery(id+"F18.opExtrude","SWEPT_EDGE",EDGE,{"disambiguationData":[OSD([subQ0,subQ1])]})]});}
            var Q1;
            Q1=makeQuery(id+"F18.opExtrude","SWEPT_EDGE",EDGE,{"disambiguationData":[OSD([sQuery(id+"F16.wireOp",EDGE,"E69.MirrorCS"),sQuery(id+"F16.wireOp",EDGE,"E70.MirrorCS")])]});
            var Q2;
            {var subQ0=sQuery(id+"F16.wireOp",EDGE,"E66.rect.top");var subQ1=sQuery(id+"F16.wireOp",EDGE,"E66.rect.right");Q2=makeQuery(id+"F18.boolean.opBoolean","MERGE",EDGE,{"derivedFrom":[makeQuery(id+"F17.opExtrude","SWEPT_EDGE",EDGE,{"disambiguationData":[OSD([subQ0,subQ1])]}),makeQuery(id+"F18.opExtrude","SWEPT_EDGE",EDGE,{"disambiguationData":[OSD([subQ0,subQ1])]})]});}
            var Q3;
            Q3=makeQuery(id+"F18.opExtrude","SWEPT_EDGE",EDGE,{"disambiguationData":[OSD([sQuery(id+"F16.wireOp",EDGE,"E70.MirrorCS"),sQuery(id+"F16.wireOp",EDGE,"E71.MirrorCS")])]});
            var Q4;
            Q4=makeQuery(id+"F18.opExtrude","SWEPT_EDGE",EDGE,{"disambiguationData":[OSD([sQuery(id+"F16.wireOp",EDGE,"E68.MirrorCS"),sQuery(id+"F16.wireOp",EDGE,"E71.MirrorCS")])]});
            var Q5;
            Q5=makeQuery(id+"F18.opExtrude","SWEPT_EDGE",EDGE,{"disambiguationData":[OSD([sQuery(id+"F16.wireOp",EDGE,"E65.rect.bottom"),sQuery(id+"F16.wireOp",EDGE,"E65.rect.right")])]});
            var Q6;
            {var subQ0=sQuery(id+"F16.wireOp",EDGE,"E66.rect.top");var subQ1=sQuery(id+"F16.wireOp",EDGE,"E66.rect.left");Q6=makeQuery(id+"F18.boolean.opBoolean","MERGE",EDGE,{"derivedFrom":[makeQuery(id+"F17.opExtrude","SWEPT_EDGE",EDGE,{"disambiguationData":[OSD([subQ0,subQ1])]}),makeQuery(id+"F18.opExtrude","SWEPT_EDGE",EDGE,{"disambiguationData":[OSD([subQ0,subQ1])]})]});}
            var Q7;
            Q7=makeQuery(id+"F18.opExtrude","SWEPT_EDGE",EDGE,{"disambiguationData":[OSD([sQuery(id+"F16.wireOp",EDGE,"E65.rect.top"),sQuery(id+"F16.wireOp",EDGE,"E65.rect.left")])]});
            var Q8;
            Q8=makeQuery(id+"F18.opExtrude","SWEPT_EDGE",EDGE,{"disambiguationData":[OSD([sQuery(id+"F16.wireOp",EDGE,"E65.rect.top"),sQuery(id+"F16.wireOp",EDGE,"E65.rect.right")])]});
            var Q9;
            Q9=makeQuery(id+"F18.opExtrude","SWEPT_EDGE",EDGE,{"disambiguationData":[OSD([sQuery(id+"F16.wireOp",EDGE,"E68.MirrorCS"),sQuery(id+"F16.wireOp",EDGE,"E69.MirrorCS")])]});
            var Q10;
            {var subQ0=sQuery(id+"F16.wireOp",EDGE,"E66.rect.bottom");var subQ1=sQuery(id+"F16.wireOp",EDGE,"E66.rect.left");Q10=makeQuery(id+"F18.boolean.opBoolean","MERGE",EDGE,{"derivedFrom":[makeQuery(id+"F17.opExtrude","SWEPT_EDGE",EDGE,{"disambiguationData":[OSD([subQ0,subQ1])]}),makeQuery(id+"F18.opExtrude","SWEPT_EDGE",EDGE,{"disambiguationData":[OSD([subQ0,subQ1])]})]});}
            var Q11;
            Q11=makeQuery(id+"F18.opExtrude","SWEPT_EDGE",EDGE,{"disambiguationData":[OSD([sQuery(id+"F16.wireOp",EDGE,"E65.rect.bottom"),sQuery(id+"F16.wireOp",EDGE,"E65.rect.left")])]});
            var Q12;
            {var subQ0=sQuery(id+"F16.wireOp",EDGE,"E72.rect.top");var subQ1=sQuery(id+"F16.wireOp",EDGE,"E72.rect.right");Q12=makeQuery(id+"F18.boolean.opBoolean","MERGE",EDGE,{"derivedFrom":[makeQuery(id+"F17.opExtrude","SWEPT_EDGE",EDGE,{"disambiguationData":[OSD([subQ0,subQ1])]}),makeQuery(id+"F18.opExtrude","SWEPT_EDGE",EDGE,{"disambiguationData":[OSD([subQ0,subQ1])]})]});}
            var Q13;
            {var subQ0=sQuery(id+"F16.wireOp",EDGE,"E72.rect.bottom");var subQ1=sQuery(id+"F16.wireOp",EDGE,"E72.rect.right");Q13=makeQuery(id+"F18.boolean.opBoolean","MERGE",EDGE,{"derivedFrom":[makeQuery(id+"F17.opExtrude","SWEPT_EDGE",EDGE,{"disambiguationData":[OSD([subQ0,subQ1])]}),makeQuery(id+"F18.opExtrude","SWEPT_EDGE",EDGE,{"disambiguationData":[OSD([subQ0,subQ1])]})]});}
            fillet(context, id + "F19", {"entities" : qUnion([Q0, Q1, Q2, Q3, Q4, Q5, Q6, Q7, Q8, Q9, Q10, Q11, Q12, Q13]), "radius" : 4 * mm, "tangentPropagation" : true, "rho" : 0.74, "crossSection" : FilletCrossSection.CONIC, "allowEdgeOverflow" : false});
        }
        {
            var Q0;
            Q0=makeQuery(id+"F18.opExtrude","CAP_EDGE",EDGE,{"disambiguationData":[OSD([sQuery(id+"F16.wireOp",EDGE,"E66.rect.top")])],"isStart":false});
            var Q1;
            Q1=makeQuery(id+"F18.opExtrude","CAP_EDGE",EDGE,{"disambiguationData":[OSD([sQuery(id+"F16.wireOp",EDGE,"E71.MirrorCS")])],"isStart":false});
            var Q2;
            Q2=makeQuery(id+"F18.opExtrude","CAP_EDGE",EDGE,{"disambiguationData":[OSD([sQuery(id+"F16.wireOp",EDGE,"E68.MirrorCS")])],"isStart":false});
            var Q3;
            Q3=makeQuery(id+"F18.opExtrude","CAP_EDGE",EDGE,{"disambiguationData":[OSD([sQuery(id+"F16.wireOp",EDGE,"E69.MirrorCS")])],"isStart":false});
            var Q4;
            Q4=makeQuery(id+"F18.opExtrude","CAP_EDGE",EDGE,{"disambiguationData":[OSD([sQuery(id+"F16.wireOp",EDGE,"E70.MirrorCS")])],"isStart":false});
            var Q5;
            Q5=makeQuery(id+"F18.opExtrude","CAP_EDGE",EDGE,{"disambiguationData":[OSD([sQuery(id+"F16.wireOp",EDGE,"E66.rect.right")])],"isStart":false});
            var Q6;
            Q6=makeQuery(id+"F18.opExtrude","CAP_EDGE",EDGE,{"disambiguationData":[OSD([sQuery(id+"F16.wireOp",EDGE,"E66.rect.bottom")])],"isStart":false});
            var Q7;
            Q7=makeQuery(id+"F18.opExtrude","CAP_EDGE",EDGE,{"disambiguationData":[OSD([sQuery(id+"F16.wireOp",EDGE,"E65.rect.top")])],"isStart":false});
            var Q8;
            Q8=makeQuery(id+"F18.opExtrude","CAP_EDGE",EDGE,{"disambiguationData":[OSD([sQuery(id+"F16.wireOp",EDGE,"E65.rect.left")])],"isStart":false});
            var Q9;
            Q9=makeQuery(id+"F18.opExtrude","CAP_FACE",FACE,{"disambiguationData":[OSD([sQuery(id+"F16.wireOp",EDGE,"E65.rect.bottom"),sQuery(id+"F16.wireOp",EDGE,"E65.rect.top"),sQuery(id+"F16.wireOp",EDGE,"E65.rect.left"),sQuery(id+"F16.wireOp",EDGE,"E65.rect.right"),sQuery(id+"F16.wireOp",EDGE,"E66.rect.bottom"),sQuery(id+"F16.wireOp",EDGE,"E66.rect.top"),sQuery(id+"F16.wireOp",EDGE,"E66.rect.left"),sQuery(id+"F16.wireOp",EDGE,"E66.rect.right"),sQuery(id+"F16.wireOp",EDGE,"E68.MirrorCS"),sQuery(id+"F16.wireOp",EDGE,"E69.MirrorCS"),sQuery(id+"F16.wireOp",EDGE,"E70.MirrorCS"),sQuery(id+"F16.wireOp",EDGE,"E71.MirrorCS")])],"isStart":false});
            fillet(context, id + "F20", {"entities" : qUnion([Q0, Q1, Q2, Q3, Q4, Q5, Q6, Q7, Q8, Q9]), "radius" : 2 * mm, "tangentPropagation" : true, "rho" : 0.8, "crossSection" : FilletCrossSection.CONIC, "allowEdgeOverflow" : false});
        }
    });
